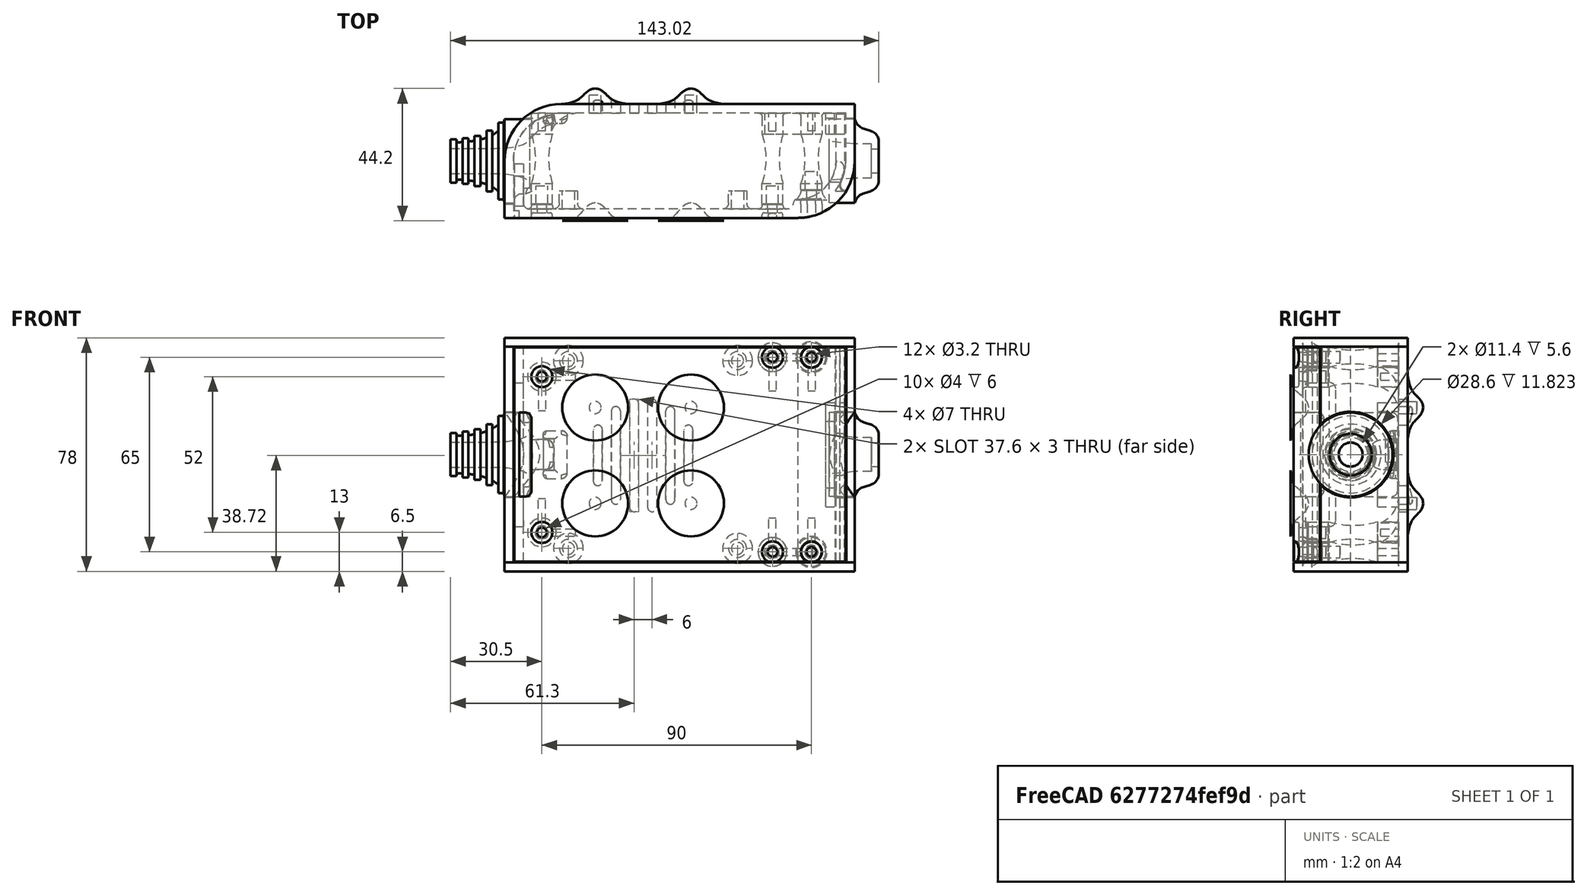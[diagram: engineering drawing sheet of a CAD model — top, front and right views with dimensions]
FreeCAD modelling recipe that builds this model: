
FCSTD DOCUMENT  (FreeCAD 0.19R0.19.2)
Label: enclosure_099
License: All rights reserved
LicenseURL: http://en.wikipedia.org/wiki/All_rights_reserved
objects: Part::Feature×72, Part::Revolution×72, Part::MultiFuse×53, Sketcher::SketchObject×30, Part::Fillet×22, Part::Cylinder×22, Part::Cut×20, Part::Extrusion×19, Part::Box×12, App::MeasureDistance×4
note: 322 computed .brp shape members not serialized (recipe doc carries the construction recipe); baked Part::Feature solids carry a one-line shape summary decoded from their .brp

FEATURE [Sketcher::SketchObject] Sketch  label="topSketch"
  FullyConstrained = true
  sketch-geometry (13):
    g0: LineSegment StartX=117 StartY=19 StartZ=0 EndX=117 EndY=38 EndZ=0
    g1: ArcOfCircle CenterX=98 CenterY=19 CenterZ=0 NormalX=0 NormalY=0 NormalZ=1 AngleXU=0 Radius=19 StartAngle=5.7297 EndAngle=6.28319
    g2: LineSegment StartX=0 StartY=3 StartZ=0 EndX=0 EndY=19 EndZ=0
    g3: LineSegment StartX=19 StartY=38 StartZ=0 EndX=117 EndY=38 EndZ=0
    g4: ArcOfCircle CenterX=19 CenterY=19 CenterZ=0 NormalX=0 NormalY=0 NormalZ=1 AngleXU=0 Radius=19 StartAngle=1.5708 EndAngle=3.14159
    g5: ArcOfCircle CenterX=19 CenterY=19 CenterZ=0 NormalX=0 NormalY=0 NormalZ=1 AngleXU=0 Radius=16 StartAngle=1.5708 EndAngle=3.14159
    g6: ArcOfCircle CenterX=98 CenterY=19 CenterZ=0 NormalX=0 NormalY=0 NormalZ=1 AngleXU=0 Radius=16 StartAngle=5.60905 EndAngle=6.28319
    g7: LineSegment StartX=114 StartY=19 StartZ=0 EndX=114 EndY=35 EndZ=0
    g8: LineSegment StartX=110.5 StartY=9.01251 StartZ=0 EndX=114.163 EndY=9.01251 EndZ=0
    g9: LineSegment StartX=114 StartY=35 StartZ=0 EndX=19 EndY=35 EndZ=0
    g10: LineSegment StartX=0 StartY=3 StartZ=0 EndX=0 EndY=0 EndZ=0
    g11: LineSegment StartX=3 StartY=0 StartZ=0 EndX=0 EndY=0 EndZ=0
    g12: LineSegment StartX=3 StartY=19 StartZ=0 EndX=3 EndY=0 EndZ=0
  constraints (33):
    c: Vertical(g0)
    c: Distance(g0) = 19
    c: Block(g0)
    c: Coincident(g1,g0)
    c: Block(g1)
    c: Vertical(g2)
    c: Block(g2)
    c: Coincident(g3,g0)
    c: Horizontal(g3)
    c: Distance(g3) = 98
    c: Coincident(g4,g3)
    c: Coincident(g4,g2)
    c: Block(g4)
    c: Coincident(g5,g4)
    c: Coincident(g6,g1)
    c: Block(g6)
    c: Block(g5)
    c: Coincident(g7,g6)
    c: Vertical(g7)
    c: Coincident(g8,g6)
    c: Coincident(g8,g1)
    c: Coincident(g9,g7)
    c: Coincident(g9,g5)
    c: Horizontal(g9)
    c: Tangent(g9,g5)
    c: Coincident(g10,g2)
    c: Distance(g10) = 3
    c: Vertical(g10)
    c: Coincident(g11,g10)
    c: Horizontal(g11)
    c: Coincident(g12,g5)
    c: Coincident(g12,g11)
    c: Vertical(g12)
FEATURE [Sketcher::SketchObject] Sketch001  label="bottomSketch"
  FullyConstrained = true
  sketch-geometry (32):
    g0: LineSegment StartX=3.3 StartY=-6.03275e-07 StartZ=0 EndX=98 EndY=-6.03275e-07 EndZ=0
    g1: ArcOfCircle CenterX=98 CenterY=19 CenterZ=0 NormalX=0 NormalY=0 NormalZ=1 AngleXU=0 Radius=19 StartAngle=4.71239 EndAngle=5.71103
    g2: LineSegment StartX=6.3 StartY=8 StartZ=0 EndX=3.3 EndY=8 EndZ=0
    g3: LineSegment StartX=3.3 StartY=8 StartZ=0 EndX=3.3 EndY=-6.03275e-07 EndZ=0
    g4: ArcOfCircle CenterX=8.3 CenterY=5 CenterZ=0 NormalX=0 NormalY=0 NormalZ=1 AngleXU=0 Radius=2 StartAngle=3.14159 EndAngle=4.71239
    g5: LineSegment StartX=6.3 StartY=8 StartZ=0 EndX=6.3 EndY=5 EndZ=0
    g6: ArcOfCircle CenterX=98 CenterY=19 CenterZ=0 NormalX=0 NormalY=0 NormalZ=1 AngleXU=0 Radius=12.7 StartAngle=4.71239 EndAngle=6.28319
    g7: LineSegment StartX=94.7 StartY=3 StartZ=0 EndX=8.3 EndY=3 EndZ=0
    g8-g12: Circle x5 (B-spline internal-alignment scaffolding for g13; pole/knot coordinates omitted)
    g13: BSplineCurve PolesCount=5 KnotsCount=3 Degree=3 IsPeriodic=0
    g14: GeomPoint X=98 Y=6.3 Z=0
    g15: GeomPoint X=96.3938 Y=4.71946 Z=0
    g16: GeomPoint X=94.7 Y=3 Z=0
    g17-g23: Circle x7 (B-spline internal-alignment scaffolding for g24; pole/knot coordinates omitted)
    g24: BSplineCurve PolesCount=7 KnotsCount=5 Degree=3 IsPeriodic=0
    g25-g29: GeomPoint x5 (B-spline internal-alignment scaffolding for g24; pole/knot coordinates omitted)
    g30: ArcOfCircle CenterX=98 CenterY=19 CenterZ=0 NormalX=0 NormalY=0 NormalZ=1 AngleXU=0 Radius=15.7 StartAngle=5.81226 EndAngle=6.28319
    g31: LineSegment StartX=110.7 StartY=19 StartZ=0 EndX=113.7 EndY=19 EndZ=0
  constraints (41):
    c: Horizontal(g0)
    c: Coincident(g1,g0)
    c: Block(g1)
    c: Horizontal(g2)
    c: Distance(g2) = 3
    c: Coincident(g3,g2)
    c: Vertical(g3)
    c: Coincident(g3,g0)
    c: Block(g4)
    c: Block(g2)
    c: Coincident(g5,g2)
    c: Coincident(g5,g4)
    c: Vertical(g5)
    c: Coincident(g6,g1)
    c: Block(g6)
    c: Coincident(g7,g4)
    c: Horizontal(g7)
    c: Block(g0)
    c: Block(g7)
    c: Block(g3)
    c: Coincident(g13,g6)
    c: Weight(g8) = 1
    c: Equal(g8, g9-g12) x4
    c: Coincident(g13,g7)
    c: InternalAlignment(g8-g12 -> g13) x5
    c: InternalAlignment(g14,g13)
    c: InternalAlignment(g15,g13)
    c: InternalAlignment(g16,g13)
    c: Block(g13)
    c: Weight(g17) = 1
    c: Equal(g17, g18-g23) x6
    c: Coincident(g24,g1)
    c: InternalAlignment(g17-g23 -> g24) x7
    c: InternalAlignment(g25-g29 -> g24) x5
    c: Block(g24)
    c: Coincident(g30,g24)
    c: Coincident(g31,g6)
    c: Coincident(g31,g30)
    c: Horizontal(g31)
    c: Block(g31)
    c: Block(g30)
FEATURE [Part::Extrusion] Extrude  label="top"
  Base = -> Sketch
  Dir = (0,0,1)
  DirMode = 2
  FaceMakerClass = Part::FaceMakerBullseye
  LengthFwd = 72
  LengthRev = 0
  Solid = true
  Symmetric = false
FEATURE [Part::Extrusion] Extrude001  label="bottom"
  Base = -> Sketch001
  Dir = (0,0,1)
  DirMode = 2
  FaceMakerClass = Part::FaceMakerBullseye
  LengthFwd = 71.4
  LengthRev = 0
  Placement = pos=(0,0,0.3) rot=(0,0,1;0rad)
  Solid = true
  Symmetric = false
FEATURE [Sketcher::SketchObject] Sketch002  label="topSketch001"
  FullyConstrained = true
  sketch-geometry (6):
    g0: LineSegment StartX=19 StartY=38 StartZ=0 EndX=117 EndY=38 EndZ=0
    g1: ArcOfCircle CenterX=19 CenterY=19 CenterZ=0 NormalX=0 NormalY=0 NormalZ=1 AngleXU=0 Radius=19 StartAngle=1.5708 EndAngle=3.14159
    g2: LineSegment StartX=117 StartY=38 StartZ=0 EndX=117 EndY=19 EndZ=0
    g3: LineSegment StartX=98 StartY=1.0161e-12 StartZ=0 EndX=5.22862e-06 EndY=1.0161e-12 EndZ=0
    g4: LineSegment StartX=5.22862e-06 StartY=19 StartZ=0 EndX=5.22862e-06 EndY=1.0161e-12 EndZ=0
    g5: ArcOfCircle CenterX=98 CenterY=19 CenterZ=0 NormalX=0 NormalY=0 NormalZ=1 AngleXU=0 Radius=19 StartAngle=4.71239 EndAngle=6.28319
  constraints (16):
    c: Horizontal(g0)
    c: Distance(g0) = 98
    c: Coincident(g1,g0)
    c: Block(g1)
    c: Coincident(g2,g0)
    c: Vertical(g2)
    c: Distance(g2) = 19
    c: Horizontal(g3)
    c: Coincident(g4,g1)
    c: Vertical(g4)
    c: Coincident(g3,g4)
    c: Block(g3)
    c: Coincident(g5,g2)
    c: Coincident(g5,g3)
    c: Block(g0)
    c: Block(g5)
FEATURE [Part::Extrusion] Extrude002  label="sideA"
  Base = -> Sketch002
  Dir = (0,0,1)
  DirMode = 2
  FaceMakerClass = Part::FaceMakerBullseye
  LengthFwd = 3
  LengthRev = 0
  Placement = pos=(0,0,-3) rot=(0,0,1;0rad)
  Solid = true
  Symmetric = false
FEATURE [Sketcher::SketchObject] Sketch003  label="topSketch002"
  FullyConstrained = true
  sketch-geometry (6):
    g0: LineSegment StartX=19 StartY=38 StartZ=0 EndX=117 EndY=38 EndZ=0
    g1: ArcOfCircle CenterX=19 CenterY=19 CenterZ=0 NormalX=0 NormalY=0 NormalZ=1 AngleXU=0 Radius=19 StartAngle=1.5708 EndAngle=3.14159
    g2: LineSegment StartX=117 StartY=38 StartZ=0 EndX=117 EndY=19 EndZ=0
    g3: LineSegment StartX=98 StartY=1.0161e-12 StartZ=0 EndX=5.22862e-06 EndY=1.0161e-12 EndZ=0
    g4: LineSegment StartX=5.22862e-06 StartY=19 StartZ=0 EndX=5.22862e-06 EndY=1.0161e-12 EndZ=0
    g5: ArcOfCircle CenterX=98 CenterY=19 CenterZ=0 NormalX=0 NormalY=0 NormalZ=1 AngleXU=0 Radius=19 StartAngle=4.71239 EndAngle=6.28319
  constraints (16):
    c: Horizontal(g0)
    c: Distance(g0) = 98
    c: Coincident(g1,g0)
    c: Block(g1)
    c: Coincident(g2,g0)
    c: Vertical(g2)
    c: Distance(g2) = 19
    c: Horizontal(g3)
    c: Coincident(g4,g1)
    c: Vertical(g4)
    c: Coincident(g3,g4)
    c: Block(g3)
    c: Coincident(g5,g2)
    c: Coincident(g5,g3)
    c: Block(g0)
    c: Block(g5)
FEATURE [Part::Extrusion] Extrude003  label="sideB"
  Base = -> Sketch003
  Dir = (0,0,1)
  DirMode = 2
  FaceMakerClass = Part::FaceMakerBullseye
  LengthFwd = 3
  LengthRev = 0
  Placement = pos=(0,0,72) rot=(0,0,1;0rad)
  Solid = true
  Symmetric = false
FEATURE [Sketcher::SketchObject] Sketch004
  FullyConstrained = true
  MapMode = 3
  Placement = pos=(0,0,0) rot=(1,0,0;1.5708rad)
  Support = -> [Extrude]
  sketch-geometry (8):
    g0: Circle CenterX=80.351 CenterY=-67.6202 CenterZ=0 NormalX=0 NormalY=0 NormalZ=1 AngleXU=0 Radius=2
    g1: Circle CenterX=80.351 CenterY=-67.6202 CenterZ=0 NormalX=0 NormalY=0 NormalZ=1 AngleXU=0 Radius=3
    g2: Circle CenterX=80.351 CenterY=-4.92017 CenterZ=0 NormalX=0 NormalY=0 NormalZ=1 AngleXU=0 Radius=2
    g3: Circle CenterX=80.351 CenterY=-4.92017 CenterZ=0 NormalX=0 NormalY=0 NormalZ=1 AngleXU=0 Radius=3
    g4: Circle CenterX=23.851 CenterY=-4.92017 CenterZ=0 NormalX=0 NormalY=0 NormalZ=1 AngleXU=0 Radius=2
    g5: Circle CenterX=23.851 CenterY=-4.92017 CenterZ=0 NormalX=0 NormalY=0 NormalZ=1 AngleXU=0 Radius=3
    g6: Circle CenterX=23.851 CenterY=-67.6202 CenterZ=0 NormalX=0 NormalY=0 NormalZ=1 AngleXU=0 Radius=2
    g7: Circle CenterX=23.851 CenterY=-67.6202 CenterZ=0 NormalX=0 NormalY=0 NormalZ=1 AngleXU=0 Radius=3
  constraints (8):
    c: Block(g3)
    c: Block(g2)
    c: Block(g1)
    c: Block(g0)
    c: Block(g6)
    c: Block(g7)
    c: Block(g4)
    c: Block(g5)
FEATURE [Part::Extrusion] Extrude004
  Base = -> Sketch004
  Dir = (0,-1,2e-16)
  DirMode = 2
  FaceMakerClass = Part::FaceMakerBullseye
  LengthFwd = 6
  LengthRev = 0
  Placement = pos=(0,9,0) rot=(0,0,1;0rad)
  Solid = true
  Symmetric = false
FEATURE [Sketcher::SketchObject] Sketch005
  FullyConstrained = true
  MapMode = 3
  Placement = pos=(0,0,0) rot=(1,0,0;1.5708rad)
  Support = -> [Extrude]
  sketch-geometry (8):
    g0: Circle CenterX=80.351 CenterY=-67.6202 CenterZ=0 NormalX=0 NormalY=0 NormalZ=1 AngleXU=0 Radius=3
    g1: Circle CenterX=80.351 CenterY=-4.92017 CenterZ=0 NormalX=0 NormalY=0 NormalZ=1 AngleXU=0 Radius=3
    g2: Circle CenterX=23.851 CenterY=-4.92017 CenterZ=0 NormalX=0 NormalY=0 NormalZ=1 AngleXU=0 Radius=3
    g3: Circle CenterX=23.851 CenterY=-67.6202 CenterZ=0 NormalX=0 NormalY=0 NormalZ=1 AngleXU=0 Radius=3
    g4: Circle CenterX=23.851 CenterY=-67.6202 CenterZ=0 NormalX=0 NormalY=0 NormalZ=1 AngleXU=0 Radius=5
    g5: Circle CenterX=80.351 CenterY=-67.6202 CenterZ=0 NormalX=0 NormalY=0 NormalZ=1 AngleXU=0 Radius=5
    g6: Circle CenterX=23.851 CenterY=-4.92017 CenterZ=0 NormalX=0 NormalY=0 NormalZ=1 AngleXU=0 Radius=5
    g7: Circle CenterX=80.351 CenterY=-4.92017 CenterZ=0 NormalX=0 NormalY=0 NormalZ=1 AngleXU=0 Radius=5
  constraints (8):
    c: Block(g1)
    c: Block(g0)
    c: Block(g3)
    c: Block(g2)
    c: Block(g5)
    c: Block(g4)
    c: Block(g6)
    c: Block(g7)
FEATURE [Part::Extrusion] Extrude005
  Base = -> Sketch005
  Dir = (0,-1,2e-16)
  DirMode = 2
  FaceMakerClass = Part::FaceMakerBullseye
  LengthFwd = 2
  LengthRev = 0
  Solid = true
  Symmetric = false
FEATURE [Sketcher::SketchObject] Sketch006
  FullyConstrained = true
  MapMode = 3
  Placement = pos=(0,0,0) rot=(1,0,0;1.5708rad)
  sketch-geometry (8):
    g0: Circle CenterX=80.351 CenterY=-67.6202 CenterZ=0 NormalX=0 NormalY=0 NormalZ=1 AngleXU=0 Radius=3
    g1: Circle CenterX=80.351 CenterY=-4.92017 CenterZ=0 NormalX=0 NormalY=0 NormalZ=1 AngleXU=0 Radius=3
    g2: Circle CenterX=23.851 CenterY=-4.92017 CenterZ=0 NormalX=0 NormalY=0 NormalZ=1 AngleXU=0 Radius=3
    g3: Circle CenterX=23.851 CenterY=-67.6202 CenterZ=0 NormalX=0 NormalY=0 NormalZ=1 AngleXU=0 Radius=3
    g4: Circle CenterX=23.851 CenterY=-67.6202 CenterZ=0 NormalX=0 NormalY=0 NormalZ=1 AngleXU=0 Radius=5
    g5: Circle CenterX=80.351 CenterY=-67.6202 CenterZ=0 NormalX=0 NormalY=0 NormalZ=1 AngleXU=0 Radius=5
    g6: Circle CenterX=23.851 CenterY=-4.92017 CenterZ=0 NormalX=0 NormalY=0 NormalZ=1 AngleXU=0 Radius=5
    g7: Circle CenterX=80.351 CenterY=-4.92017 CenterZ=0 NormalX=0 NormalY=0 NormalZ=1 AngleXU=0 Radius=5
  constraints (8):
    c: Block(g1)
    c: Block(g0)
    c: Block(g3)
    c: Block(g2)
    c: Block(g5)
    c: Block(g4)
    c: Block(g6)
    c: Block(g7)
FEATURE [Part::Extrusion] Extrude007
  Base = -> Sketch006
  Dir = (0,-1,2e-16)
  DirMode = 2
  FaceMakerClass = Part::FaceMakerBullseye
  LengthFwd = 2
  LengthRev = 0
  Solid = true
  Symmetric = false
FEATURE [Part::Fillet] Fillet
  Base = -> Extrude007
  Edges = 4 edges r=1.99: [Edge6,Edge12,Edge18,Edge24]
FEATURE [Part::Cut] Cut
  Base = -> Extrude005
  Placement = pos=(0,5,0) rot=(0,0,1;0rad)
  Tool = -> Fillet
FEATURE [Part::MultiFuse] Fusion  label="pCBScrews"
  Placement = pos=(-2.5,0,72.3) rot=(0,0,1;0rad)
  Shapes = -> [Extrude004,Cut]
FEATURE [App::MeasureDistance] Distance  label="Distance: 0.69 mm"
  Distance = 0.685967
  P1 = (24.0138,2.9647,0.3)
  P2 = (23.8901,3,-0.373787)
FEATURE [App::MeasureDistance] Distance001  label="Distance: 0.53 mm"
  Distance = 0.533607
  P1 = (80.2939,3,72.2334)
  P2 = (80.281,2.99661,71.7)
FEATURE [Part::Fillet] Fillet001
  Base = -> Extrude001
  Edges = 1 edges r=2.4: [Edge17]
FEATURE [Part::Fillet] Fillet002  label="bottom001"
  Base = -> Fillet001
  Edges = 1 edges r=2.4: [Edge36]
FEATURE [Part::Fillet] Fillet003  label="top001"
  Base = -> Extrude
  Edges = 1 edges r=2: [Edge1]
FEATURE [Sketcher::SketchObject] Sketch007
  FullyConstrained = true
  sketch-geometry (16):
    g0: LineSegment StartX=4 StartY=0 StartZ=0 EndX=4 EndY=2.4 EndZ=0
    g1: LineSegment StartX=4 StartY=2.4 StartZ=0 EndX=7 EndY=2.4 EndZ=0
    g2: LineSegment StartX=4 StartY=0 StartZ=0 EndX=5.7 EndY=0 EndZ=0
    g3: LineSegment StartX=5.7 StartY=0 StartZ=0 EndX=5.7 EndY=-5.6 EndZ=0
    g4-g8: Circle x5 (B-spline internal-alignment scaffolding for g9; pole/knot coordinates omitted)
    g9: BSplineCurve PolesCount=5 KnotsCount=3 Degree=3 IsPeriodic=0
    g10: GeomPoint X=7 Y=2.4 Z=0
    g11: GeomPoint X=10.4582 Y=-1.55472 Z=0
    g12: GeomPoint X=14 Y=-5.6 Z=0
    g13: LineSegment StartX=14 StartY=-5.6 StartZ=0 EndX=14 EndY=-14.1 EndZ=0
    g14: LineSegment StartX=14 StartY=-14.1 StartZ=0 EndX=6.5 EndY=-14.1 EndZ=0
    g15: LineSegment StartX=5.7 StartY=-5.6 StartZ=0 EndX=6.5 EndY=-14.1 EndZ=0
  constraints (28):
    c: Distance(g0) = 2.4
    c: Vertical(g0)
    c: Block(g0)
    c: Coincident(g1,g0)
    c: Horizontal(g1)
    c: Distance(g1) = 3
    c: Coincident(g2,g0)
    c: Horizontal(g2)
    c: Distance(g2) = 1.7
    c: Coincident(g3,g2)
    c: Vertical(g3)
    c: Distance(g3) = 5.6
    c: Coincident(g9,g1)
    c: Weight(g4) = 1
    c: Equal(g4, g5-g8) x4
    c: InternalAlignment(g4-g8 -> g9) x5
    c: InternalAlignment(g10,g9)
    c: InternalAlignment(g11,g9)
    c: InternalAlignment(g12,g9)
    c: Block(g9)
    c: Coincident(g13,g9)
    c: Vertical(g13)
    c: Distance(g13) = 8.5
    c: Coincident(g14,g13)
    c: Horizontal(g14)
    c: Distance(g14) = 7.5
    c: Coincident(g15,g3)
    c: Coincident(g15,g14)
FEATURE [Part::Feature] Face
  shape: bbox 10 x 16.5 x 2e-07 mm, 1 faces, 0 solids (baked)
FEATURE [Part::Revolution] Revolve  label="plugHousing"
  Angle = 360
  Axis = (0,1,0)
  Base = (0,0,0)
  FaceMakerClass = Part::FaceMakerBullseye
  Placement = pos=(0,0,36.15) rot=(0,0,1;0rad)
  Solid = false
  Source = -> Face
  Symmetric = false
FEATURE [Part::Feature] Face001
  shape: bbox 10 x 16.5 x 2e-07 mm, 1 faces, 0 solids (baked)
FEATURE [Part::Revolution] Revolve001  label="plugHousing001"
  Angle = 360
  Axis = (0,1,0)
  Base = (0,0,0)
  FaceMakerClass = Part::FaceMakerBullseye
  Placement = pos=(0,0,36.15) rot=(0,0,1;0rad)
  Solid = false
  Source = -> Face001
  Symmetric = false
FEATURE [Part::MultiFuse] Fusion001  label="plugHousing002"
  Placement = pos=(0,0,0) rot=(0,0,1;1.5708rad)
  Shapes = -> [Revolve001,Revolve]
FEATURE [Part::Feature] Face002
  shape: bbox 10 x 16.5 x 2e-07 mm, 1 faces, 0 solids (baked)
FEATURE [Part::Revolution] Revolve003  label="plugHousing005"
  Angle = 360
  Axis = (0,1,0)
  Base = (0,0,0)
  FaceMakerClass = Part::FaceMakerBullseye
  Placement = pos=(0,0,36.15) rot=(0,0,1;0rad)
  Solid = false
  Source = -> Face002
  Symmetric = false
FEATURE [Part::Feature] Face003
  shape: bbox 10 x 16.5 x 2e-07 mm, 1 faces, 0 solids (baked)
FEATURE [Part::Revolution] Revolve002  label="plugHousing003"
  Angle = 360
  Axis = (0,1,0)
  Base = (0,0,0)
  FaceMakerClass = Part::FaceMakerBullseye
  Placement = pos=(0,0,36.15) rot=(0,0,1;0rad)
  Solid = false
  Source = -> Face003
  Symmetric = false
FEATURE [Part::MultiFuse] Fusion002  label="plugHousing004"
  Placement = pos=(0,0,0) rot=(0,0,1;1.5708rad)
  Shapes = -> [Revolve002,Revolve003]
FEATURE [Part::MultiFuse] Fusion003  label="plugHousing006"
  Placement = pos=(0,19,0) rot=(0,0,1;3.14159rad)
  Shapes = -> [Fusion002,Fusion001]
FEATURE [Part::Feature] Face004
  shape: bbox 10 x 16.5 x 2e-07 mm, 1 faces, 0 solids (baked)
FEATURE [Part::Revolution] Revolve006  label="plugHousing010"
  Angle = 360
  Axis = (0,1,0)
  Base = (0,0,0)
  FaceMakerClass = Part::FaceMakerBullseye
  Placement = pos=(0,0,36.15) rot=(0,0,1;0rad)
  Solid = false
  Source = -> Face004
  Symmetric = false
FEATURE [Part::Feature] Face005
  shape: bbox 10 x 16.5 x 2e-07 mm, 1 faces, 0 solids (baked)
FEATURE [Part::Revolution] Revolve007  label="plugHousing011"
  Angle = 360
  Axis = (0,1,0)
  Base = (0,0,0)
  FaceMakerClass = Part::FaceMakerBullseye
  Placement = pos=(0,0,36.15) rot=(0,0,1;0rad)
  Solid = false
  Source = -> Face005
  Symmetric = false
FEATURE [Part::Feature] Face006
  shape: bbox 10 x 16.5 x 2e-07 mm, 1 faces, 0 solids (baked)
FEATURE [Part::Revolution] Revolve004  label="plugHousing007"
  Angle = 360
  Axis = (0,1,0)
  Base = (0,0,0)
  FaceMakerClass = Part::FaceMakerBullseye
  Placement = pos=(0,0,36.15) rot=(0,0,1;0rad)
  Solid = false
  Source = -> Face006
  Symmetric = false
FEATURE [Part::MultiFuse] Fusion004  label="plugHousing009"
  Placement = pos=(0,0,0) rot=(0,0,1;1.5708rad)
  Shapes = -> [Revolve004,Revolve007]
FEATURE [Part::Feature] Face007
  shape: bbox 10 x 16.5 x 2e-07 mm, 1 faces, 0 solids (baked)
FEATURE [Part::Revolution] Revolve005  label="plugHousing008"
  Angle = 360
  Axis = (0,1,0)
  Base = (0,0,0)
  FaceMakerClass = Part::FaceMakerBullseye
  Placement = pos=(0,0,36.15) rot=(0,0,1;0rad)
  Solid = false
  Source = -> Face007
  Symmetric = false
FEATURE [Part::MultiFuse] Fusion005  label="plugHousing012"
  Placement = pos=(0,0,0) rot=(0,0,1;1.5708rad)
  Shapes = -> [Revolve006,Revolve005]
FEATURE [Part::MultiFuse] Fusion006  label="plugHousing013"
  Placement = pos=(0,19,0) rot=(0,0,1;3.14159rad)
  Shapes = -> [Fusion005,Fusion004]
FEATURE [Part::MultiFuse] Fusion007  label="plugHousing014"
  Placement = pos=(122.621,0,-0.15) rot=(0,0,1;0rad)
  Shapes = -> [Fusion003,Fusion006]
FEATURE [Part::Cylinder] Cylinder002
  Angle = 360
  AttacherType = Attacher::AttachEngine3D
  Height = 20
  Placement = pos=(0,0,36.15) rot=(0,0,1;0rad)
  Radius = 4
FEATURE [Part::Cylinder] Cylinder003
  Angle = 360
  AttacherType = Attacher::AttachEngine3D
  Height = 10
  Placement = pos=(0,0,36.15) rot=(0,0,1;0rad)
  Radius = 4
FEATURE [Part::MultiFuse] Fusion009  label="removeToCreateHoleForPlugHousing"
  Placement = pos=(70,19,36.15) rot=(0,1,0;1.5708rad)
  Shapes = -> [Cylinder002,Cylinder003]
FEATURE [Part::Cylinder] Cylinder004
  Angle = 360
  AttacherType = Attacher::AttachEngine3D
  Height = 20
  Placement = pos=(0,0,36.15) rot=(0,0,1;0rad)
  Radius = 4
FEATURE [Part::Cylinder] Cylinder005
  Angle = 360
  AttacherType = Attacher::AttachEngine3D
  Height = 10
  Placement = pos=(0,0,36.15) rot=(0,0,1;0rad)
  Radius = 4
FEATURE [Part::MultiFuse] Fusion010  label="removeToCreateHoleForPlugHousing001"
  Placement = pos=(70,19,36.15) rot=(0,1,0;1.5708rad)
  Shapes = -> [Cylinder004,Cylinder005]
FEATURE [Part::Cut] Cut001
  Base = -> Fillet003
  Tool = -> Fusion010
FEATURE [Part::Cut] Cut002  label="Bottom"
  Base = -> Fillet002
  Tool = -> Fusion009
FEATURE [Part::Feature] Face008
  shape: bbox 10 x 16.5 x 2e-07 mm, 1 faces, 0 solids (baked)
FEATURE [Part::Revolution] Revolve011  label="plugHousing021"
  Angle = 360
  Axis = (0,1,0)
  Base = (0,0,0)
  FaceMakerClass = Part::FaceMakerBullseye
  Placement = pos=(0,0,36.15) rot=(0,0,1;0rad)
  Solid = false
  Source = -> Face008
  Symmetric = false
FEATURE [Part::Feature] Face009
  shape: bbox 10 x 16.5 x 2e-07 mm, 1 faces, 0 solids (baked)
FEATURE [Part::Revolution] Revolve012  label="plugHousing022"
  Angle = 360
  Axis = (0,1,0)
  Base = (0,0,0)
  FaceMakerClass = Part::FaceMakerBullseye
  Placement = pos=(0,0,36.15) rot=(0,0,1;0rad)
  Solid = false
  Source = -> Face009
  Symmetric = false
FEATURE [Part::Feature] Face010 .. Face013  x4 (patterned run collapsed; names and placements below)
  shape: bbox 10 x 16.5 x 2e-07 mm, 1 faces, 0 solids (baked)
FEATURE [Part::Revolution] Revolve015  label="plugHousing027"
  Angle = 360
  Axis = (0,1,0)
  Base = (0,0,0)
  FaceMakerClass = Part::FaceMakerBullseye
  Placement = pos=(0,0,36.15) rot=(0,0,1;0rad)
  Solid = false
  Source = -> Face013
  Symmetric = false
FEATURE [Part::Feature] Face014
  shape: bbox 10 x 16.5 x 2e-07 mm, 1 faces, 0 solids (baked)
FEATURE [Part::Feature] Face015
  shape: bbox 10 x 16.5 x 2e-07 mm, 1 faces, 0 solids (baked)
FEATURE [Part::Feature] Face016
  shape: bbox 10 x 16.5 x 2e-07 mm, 1 faces, 0 solids (baked)
FEATURE [Part::Revolution] Revolve019  label="plugHousing033"
  Angle = 360
  Axis = (0,1,0)
  Base = (0,0,0)
  FaceMakerClass = Part::FaceMakerBullseye
  Placement = pos=(0,0,36.15) rot=(0,0,1;0rad)
  Solid = false
  Source = -> Face016
  Symmetric = false
FEATURE [Part::Feature] Face017
  shape: bbox 10 x 16.5 x 2e-07 mm, 1 faces, 0 solids (baked)
FEATURE [Part::Revolution] Revolve020  label="plugHousing034"
  Angle = 360
  Axis = (0,1,0)
  Base = (0,0,0)
  FaceMakerClass = Part::FaceMakerBullseye
  Placement = pos=(0,0,36.15) rot=(0,0,1;0rad)
  Solid = false
  Source = -> Face017
  Symmetric = false
FEATURE [Part::Feature] Face018
  shape: bbox 10 x 16.5 x 2e-07 mm, 1 faces, 0 solids (baked)
FEATURE [Part::Revolution] Revolve016  label="plugHousing030"
  Angle = 360
  Axis = (0,1,0)
  Base = (0,0,0)
  FaceMakerClass = Part::FaceMakerBullseye
  Placement = pos=(0,0,36.15) rot=(0,0,1;0rad)
  Solid = false
  Source = -> Face018
  Symmetric = false
FEATURE [Part::MultiFuse] Fusion020  label="plugHousing038"
  Placement = pos=(0,0,0) rot=(0,0,1;1.5708rad)
  Shapes = -> [Revolve016,Revolve020]
FEATURE [Part::Feature] Face019
  shape: bbox 10 x 16.5 x 2e-07 mm, 1 faces, 0 solids (baked)
FEATURE [Part::Feature] Face020
  shape: bbox 10 x 16.5 x 2e-07 mm, 1 faces, 0 solids (baked)
FEATURE [Part::Revolution] Revolve017  label="plugHousing031"
  Angle = 360
  Axis = (0,1,0)
  Base = (0,0,0)
  FaceMakerClass = Part::FaceMakerBullseye
  Placement = pos=(0,0,36.15) rot=(0,0,1;0rad)
  Solid = false
  Source = -> Face020
  Symmetric = false
FEATURE [Part::MultiFuse] Fusion021  label="plugHousing039"
  Placement = pos=(0,0,0) rot=(0,0,1;1.5708rad)
  Shapes = -> [Revolve019,Revolve017]
FEATURE [Part::MultiFuse] Fusion023  label="plugHousing041"
  Placement = pos=(0,19,0) rot=(0,0,1;3.14159rad)
  Shapes = -> [Fusion021,Fusion020]
FEATURE [Part::Revolution] Revolve022  label="plugHousing043"
  Angle = 360
  Axis = (0,1,0)
  Base = (0,0,0)
  FaceMakerClass = Part::FaceMakerBullseye
  Placement = pos=(0,0,36.15) rot=(0,0,1;0rad)
  Solid = false
  Source = -> Face019
  Symmetric = false
FEATURE [Part::Feature] Face021
  shape: bbox 10 x 16.5 x 2e-07 mm, 1 faces, 0 solids (baked)
FEATURE [Part::Revolution] Revolve023  label="plugHousing044"
  Angle = 360
  Axis = (0,1,0)
  Base = (0,0,0)
  FaceMakerClass = Part::FaceMakerBullseye
  Placement = pos=(0,0,36.15) rot=(0,0,1;0rad)
  Solid = false
  Source = -> Face021
  Symmetric = false
FEATURE [Part::Feature] Face022
  shape: bbox 10 x 16.5 x 2e-07 mm, 1 faces, 0 solids (baked)
FEATURE [Part::Revolution] Revolve018  label="plugHousing032"
  Angle = 360
  Axis = (0,1,0)
  Base = (0,0,0)
  FaceMakerClass = Part::FaceMakerBullseye
  Placement = pos=(0,0,36.15) rot=(0,0,1;0rad)
  Solid = false
  Source = -> Face022
  Symmetric = false
FEATURE [Part::MultiFuse] Fusion022  label="plugHousing040"
  Placement = pos=(0,0,0) rot=(0,0,1;1.5708rad)
  Shapes = -> [Revolve018,Revolve023]
FEATURE [Part::Feature] Face023
  shape: bbox 10 x 16.5 x 2e-07 mm, 1 faces, 0 solids (baked)
FEATURE [Part::Revolution] Revolve021  label="plugHousing035"
  Angle = 360
  Axis = (0,1,0)
  Base = (0,0,0)
  FaceMakerClass = Part::FaceMakerBullseye
  Placement = pos=(0,0,36.15) rot=(0,0,1;0rad)
  Solid = false
  Source = -> Face023
  Symmetric = false
FEATURE [Part::MultiFuse] Fusion018  label="plugHousing036"
  Placement = pos=(0,0,0) rot=(0,0,1;1.5708rad)
  Shapes = -> [Revolve022,Revolve021]
FEATURE [Part::MultiFuse] Fusion019  label="plugHousing037"
  Placement = pos=(0,19,0) rot=(0,0,1;3.14159rad)
  Shapes = -> [Fusion018,Fusion022]
FEATURE [Part::MultiFuse] Fusion024  label="plugHousing042"
  Placement = pos=(122.621,0,-0.15) rot=(0,0,1;0rad)
  Shapes = -> [Fusion023,Fusion019]
FEATURE [Part::Cylinder] Cylinder006
  Angle = 360
  AttacherType = Attacher::AttachEngine3D
  Height = 20
  Placement = pos=(0,0,36.15) rot=(0,0,1;0rad)
  Radius = 14.3
FEATURE [Part::Cylinder] Cylinder007
  Angle = 360
  AttacherType = Attacher::AttachEngine3D
  Height = 10
  Placement = pos=(0,0,36.15) rot=(0,0,1;0rad)
  Radius = 4
FEATURE [Part::MultiFuse] Fusion026  label="removeToCreteHoleForPlugHousing"
  Placement = pos=(70,19,36) rot=(0,1,0;1.5708rad)
  Shapes = -> [Cylinder006,Cylinder007]
FEATURE [Part::Box] Box001  label="Cube001"
  AttacherType = Attacher::AttachEngine3D
  Height = 28
  Length = 3
  Placement = pos=(110.7,19,22) rot=(0,0,1;0rad)
  Width = 15.7
FEATURE [Part::Cut] Cut003  label="top002"
  Base = -> Cut001
  Tool = -> Fusion007
FEATURE [Part::Revolution] Revolve008  label="plugHousing015"
  Angle = 360
  Axis = (0,1,0)
  Base = (0,0,0)
  FaceMakerClass = Part::FaceMakerBullseye
  Placement = pos=(0,0,36.15) rot=(0,0,1;0rad)
  Solid = false
  Source = -> Face010
  Symmetric = false
FEATURE [Part::MultiFuse] Fusion013  label="plugHousing020"
  Placement = pos=(0,0,0) rot=(0,0,1;1.5708rad)
  Shapes = -> [Revolve008,Revolve012]
FEATURE [Part::Cut] Cut004  label="top003"
  Base = -> Cut003
  Placement = pos=(1,0,0) rot=(0,0,1;0rad)
  Tool = -> Fusion026
FEATURE [Part::Cylinder] Cylinder008
  Angle = 360
  AttacherType = Attacher::AttachEngine3D
  Height = 20
  Placement = pos=(0,0,36.15) rot=(0,0,1;0rad)
  Radius = 10.3
FEATURE [Part::Cylinder] Cylinder009
  Angle = 360
  AttacherType = Attacher::AttachEngine3D
  Height = 10
  Placement = pos=(0,0,36.15) rot=(0,0,1;0rad)
  Radius = 4
FEATURE [Part::MultiFuse] Fusion027  label="removeToCreteHoleForPlugHousing001"
  Placement = pos=(70,19,36) rot=(0,1,0;1.5708rad)
  Shapes = -> [Cylinder008,Cylinder009]
FEATURE [Part::Cut] Cut005  label="plugHousingTab"
  Base = -> Box001
  Tool = -> Fusion027
FEATURE [Part::MultiFuse] Fusion028  label="plugHousing045"
  Shapes = -> [Fusion024,Cut005]
FEATURE [Part::Box] Box002  label="Cube002"
  AttacherType = Attacher::AttachEngine3D
  Height = 28.8
  Length = 3
  Placement = pos=(107.3,28,21.6) rot=(0,0,1;0rad)
  Width = 7
FEATURE [Part::Box] Box003  label="Cube003"
  AttacherType = Attacher::AttachEngine3D
  Height = 3
  Length = 6.4
  Placement = pos=(107.3,28,18.6) rot=(0,0,1;0rad)
  Width = 7
FEATURE [Part::Box] Box004  label="Cube004"
  AttacherType = Attacher::AttachEngine3D
  Height = 3
  Length = 6.4
  Placement = pos=(107.3,28,50.4) rot=(0,0,1;0rad)
  Width = 7
FEATURE [Part::MultiFuse] Fusion029  label="plugHousingBracketHolder"
  Shapes = -> [Box004,Box002,Box003]
FEATURE [Part::Cylinder] Cylinder010
  Angle = 360
  AttacherType = Attacher::AttachEngine3D
  Height = 20
  Placement = pos=(0,0,36.15) rot=(0,0,1;0rad)
  Radius = 14.3
FEATURE [Part::Cylinder] Cylinder011
  Angle = 360
  AttacherType = Attacher::AttachEngine3D
  Height = 10
  Placement = pos=(0,0,36.15) rot=(0,0,1;0rad)
  Radius = 4
FEATURE [Part::MultiFuse] Fusion030  label="removeToCreteHoleForPlugHousing002"
  Placement = pos=(70,19,36) rot=(0,1,0;1.5708rad)
  Shapes = -> [Cylinder010,Cylinder011]
FEATURE [Part::Cut] Cut006  label="plugHousingBracketHolder001"
  Base = -> Fusion029
  Tool = -> Fusion030
FEATURE [Part::Cylinder] Cylinder012
  Angle = 360
  AttacherType = Attacher::AttachEngine3D
  Height = 20
  Placement = pos=(0,0,36.15) rot=(0,0,1;0rad)
  Radius = 7
FEATURE [Part::Cylinder] Cylinder013
  Angle = 360
  AttacherType = Attacher::AttachEngine3D
  Height = 10
  Placement = pos=(0,0,36.15) rot=(0,0,1;0rad)
  Radius = 4
FEATURE [Part::MultiFuse] Fusion032  label="removeToCreteHoleForPlugHousing003"
  Placement = pos=(70,19,36) rot=(0,1,0;1.5708rad)
  Shapes = -> [Cylinder012,Cylinder013]
FEATURE [Part::Cut] Cut007  label="bottom002"
  Base = -> Cut002
  Tool = -> Fusion032
FEATURE [Sketcher::SketchObject] Sketch008
  FullyConstrained = true
  sketch-geometry (54):
    g0: LineSegment StartX=-4.2 StartY=0 StartZ=0 EndX=-6.2 EndY=0 EndZ=0
    g1: LineSegment StartX=-14 StartY=-18 StartZ=0 EndX=-14 EndY=-26.5 EndZ=0
    g2: LineSegment StartX=-4.2 StartY=0 StartZ=0 EndX=-4.2 EndY=-13.4877 EndZ=0
    g3: Circle CenterX=-4.2 CenterY=-13.4877 CenterZ=0 NormalX=0 NormalY=0 NormalZ=1 AngleXU=0 Radius=1
    g4: Circle CenterX=-4.2 CenterY=-26.5 CenterZ=0 NormalX=0 NormalY=0 NormalZ=1 AngleXU=0 Radius=1
    g5: Circle CenterX=-8.2 CenterY=-26.5 CenterZ=0 NormalX=0 NormalY=0 NormalZ=1 AngleXU=0 Radius=1
    g6: BSplineCurve PolesCount=3 KnotsCount=2 Degree=2 IsPeriodic=0
    g7: GeomPoint X=-4.2 Y=-13.4877 Z=0
    g8: GeomPoint X=-8.2 Y=-26.5 Z=0
    g9: LineSegment StartX=-14 StartY=-26.5 StartZ=0 EndX=-8.2 EndY=-26.5 EndZ=0
    g10: LineSegment StartX=-10.15 StartY=-12 StartZ=0 EndX=-10.15 EndY=-14 EndZ=0
    g11: LineSegment StartX=-12.8401 StartY=-16 StartZ=0 EndX=-10.1571 EndY=-16 EndZ=0
    g12: LineSegment StartX=-10.15 StartY=-14 StartZ=0 EndX=-8.70761 EndY=-14 EndZ=0
    g13: LineSegment StartX=-12.8401 StartY=-16 StartZ=0 EndX=-12.8401 EndY=-17.6958 EndZ=0
    g14: LineSegment StartX=-10.15 StartY=-12 StartZ=0 EndX=-7.79258 EndY=-12 EndZ=0
    g15: Circle CenterX=-6.2215 CenterY=-2 CenterZ=0 NormalX=0 NormalY=0 NormalZ=1 AngleXU=0 Radius=1
    g16: Circle CenterX=-6.22762 CenterY=-2.58724 CenterZ=0 NormalX=0 NormalY=0 NormalZ=1 AngleXU=0 Radius=1
    g17: Circle CenterX=-6.32538 CenterY=-4 CenterZ=0 NormalX=0 NormalY=0 NormalZ=1 AngleXU=0 Radius=1
    g18: BSplineCurve PolesCount=3 KnotsCount=2 Degree=2 IsPeriodic=0
    g19: GeomPoint X=-6.2215 Y=-2 Z=0
    g20: GeomPoint X=-6.32538 Y=-4 Z=0
    g21: Circle CenterX=-6.48644 CenterY=-5.99526 CenterZ=0 NormalX=0 NormalY=0 NormalZ=1 AngleXU=0 Radius=1
    g22: Circle CenterX=-6.58486 CenterY=-6.99526 CenterZ=0 NormalX=0 NormalY=0 NormalZ=1 AngleXU=0 Radius=1
    g23: Circle CenterX=-6.77343 CenterY=-8 CenterZ=0 NormalX=0 NormalY=0 NormalZ=1 AngleXU=0 Radius=1
    g24: BSplineCurve PolesCount=3 KnotsCount=2 Degree=2 IsPeriodic=0
    g25: GeomPoint X=-6.48644 Y=-5.99526 Z=0
    g26: GeomPoint X=-6.77343 Y=-8 Z=0
    g27: Circle CenterX=-7.19003 CenterY=-10 CenterZ=0 NormalX=0 NormalY=0 NormalZ=1 AngleXU=0 Radius=1
    g28: Circle CenterX=-7.44407 CenterY=-11.0915 CenterZ=0 NormalX=0 NormalY=0 NormalZ=1 AngleXU=0 Radius=1
    g29: Circle CenterX=-7.79258 CenterY=-12 CenterZ=0 NormalX=0 NormalY=0 NormalZ=1 AngleXU=0 Radius=1
    g30: BSplineCurve PolesCount=3 KnotsCount=2 Degree=2 IsPeriodic=0
    g31: GeomPoint X=-7.19003 Y=-10 Z=0
    g32: GeomPoint X=-7.79258 Y=-12 Z=0
    g33: Circle CenterX=-8.70761 CenterY=-14 CenterZ=0 NormalX=0 NormalY=0 NormalZ=1 AngleXU=0 Radius=1
    g34: Circle CenterX=-9.33087 CenterY=-15.1837 CenterZ=0 NormalX=0 NormalY=0 NormalZ=1 AngleXU=0 Radius=1
    g35: Circle CenterX=-10.1571 CenterY=-16 CenterZ=0 NormalX=0 NormalY=0 NormalZ=1 AngleXU=0 Radius=1
    g36: BSplineCurve PolesCount=3 KnotsCount=2 Degree=2 IsPeriodic=0
    g37: GeomPoint X=-8.70761 Y=-14 Z=0
    g38: GeomPoint X=-10.1571 Y=-16 Z=0
    g39: Circle CenterX=-12.8401 CenterY=-17.6958 CenterZ=0 NormalX=0 NormalY=0 NormalZ=1 AngleXU=0 Radius=1
    g40: Circle CenterX=-13.3521 CenterY=-17.9027 CenterZ=0 NormalX=0 NormalY=0 NormalZ=1 AngleXU=0 Radius=1
    g41: Circle CenterX=-14 CenterY=-18 CenterZ=0 NormalX=0 NormalY=0 NormalZ=1 AngleXU=0 Radius=1
    g42: BSplineCurve PolesCount=3 KnotsCount=2 Degree=2 IsPeriodic=0
    g43: GeomPoint X=-12.8401 Y=-17.6958 Z=0
    g44: GeomPoint X=-14 Y=-18 Z=0
    g45: LineSegment StartX=-6.2 StartY=0 StartZ=0 EndX=-7.2 EndY=0 EndZ=0
    g46: LineSegment StartX=-7.2 StartY=0 StartZ=0 EndX=-7.2 EndY=-2 EndZ=0
    g47: LineSegment StartX=-7.2 StartY=-2 StartZ=0 EndX=-6.2215 EndY=-2 EndZ=0
    g48: LineSegment StartX=-6.32538 StartY=-4 StartZ=0 EndX=-7.65538 EndY=-4 EndZ=0
    g49: LineSegment StartX=-7.65538 StartY=-4 StartZ=0 EndX=-7.65538 EndY=-5.99526 EndZ=0
    g50: LineSegment StartX=-7.65538 StartY=-5.99526 StartZ=0 EndX=-6.48644 EndY=-5.99526 EndZ=0
    g51: LineSegment StartX=-6.77343 StartY=-8 StartZ=0 EndX=-8.43343 EndY=-8 EndZ=0
    g52: LineSegment StartX=-8.43343 StartY=-8 StartZ=0 EndX=-8.43343 EndY=-10 EndZ=0
    g53: LineSegment StartX=-8.43343 StartY=-10 StartZ=0 EndX=-7.19003 EndY=-10 EndZ=0
  constraints (112):
    c: Horizontal(g0)
    c: Distance(g0) = 2
    c: Block(g0)
    c: Vertical(g1)
    c: Coincident(g2,g0)
    c: Vertical(g2)
    c: Block(g2)
    c: Coincident(g6,g2)
    c: Weight(g3) = 1
    c: Equal(g3,g4)
    c: Equal(g3,g5)
    c: InternalAlignment(g3,g6)
    c: InternalAlignment(g4,g6)
    c: InternalAlignment(g5,g6)
    c: InternalAlignment(g7,g6)
    c: InternalAlignment(g8,g6)
    c: Block(g6)
    c: Coincident(g9,g1)
    c: Coincident(g9,g6)
    c: Horizontal(g9)
    c: Vertical(g10)
    c: Block(g10)
    c: Horizontal(g11)
    c: Block(g11)
    c: Coincident(g12,g10)
    c: Horizontal(g12)
    c: Block(g12)
    c: Coincident(g13,g11)
    c: Vertical(g13)
    c: Block(g13)
    c: Coincident(g14,g10)
    c: Horizontal(g14)
    c: Block(g14)
    c: Block(g9)
    c: Block(g1)
    c: Weight(g15) = 1
    c: Equal(g15,g16)
    c: Equal(g15,g17)
    c: InternalAlignment(g15,g18)
    c: InternalAlignment(g16,g18)
    c: InternalAlignment(g17,g18)
    c: InternalAlignment(g19,g18)
    c: InternalAlignment(g20,g18)
    c: Weight(g21) = 1
    c: Equal(g21,g22)
    c: Equal(g21,g23)
    c: InternalAlignment(g21,g24)
    c: InternalAlignment(g22,g24)
    c: InternalAlignment(g23,g24)
    c: InternalAlignment(g25,g24)
    c: InternalAlignment(g26,g24)
    c: Weight(g27) = 1
    c: Equal(g27,g28)
    c: Equal(g27,g29)
    c: Coincident(g30,g14)
    c: InternalAlignment(g27,g30)
    c: InternalAlignment(g28,g30)
    c: InternalAlignment(g29,g30)
    c: InternalAlignment(g31,g30)
    c: InternalAlignment(g32,g30)
    c: Coincident(g36,g12)
    c: Weight(g33) = 1
    c: Equal(g33,g34)
    c: Equal(g33,g35)
    c: Coincident(g36,g11)
    c: InternalAlignment(g33,g36)
    c: InternalAlignment(g34,g36)
    c: InternalAlignment(g35,g36)
    c: InternalAlignment(g37,g36)
    c: InternalAlignment(g38,g36)
    c: Coincident(g42,g13)
    c: Weight(g39) = 1
    c: Equal(g39,g40)
    c: Equal(g39,g41)
    c: Coincident(g42,g1)
    c: InternalAlignment(g39,g42)
    c: InternalAlignment(g40,g42)
    c: InternalAlignment(g41,g42)
    c: InternalAlignment(g43,g42)
    c: InternalAlignment(g44,g42)
    c: Block(g18)
    c: Block(g24)
    c: Block(g30)
    c: Block(g36)
    c: Block(g42)
    c: Horizontal(g45)
    c: Coincident(g45,g0)
    c: Vertical(g46)
    c: Coincident(g46,g45)
    c: Coincident(g47,g46)
    c: Coincident(g47,g18)
    c: Horizontal(g47)
    c: Block(g46)
    c: Coincident(g48,g18)
    c: Horizontal(g48)
    c: Distance(g48) = 1.33
    c: Vertical(g49)
    c: Coincident(g49,g48)
    c: Coincident(g50,g49)
    c: Coincident(g50,g24)
    c: Horizontal(g50)
    c: Tangent(g50,g22)
    c: Horizontal(g51)
    c: Coincident(g51,g24)
    c: Block(g51)
    c: Vertical(g52)
    c: Block(g52)
    c: Coincident(g52,g51)
    c: Coincident(g53,g52)
    c: Coincident(g53,g30)
    c: Horizontal(g53)
    c: Distance(g1) = 8.5
FEATURE [Part::Feature] Face024
  shape: bbox 9.8 x 26.5 x 2e-07 mm, 1 faces, 0 solids (baked)
FEATURE [Part::Revolution] Revolve024
  Angle = 360
  Axis = (0,1,0)
  Base = (0,0,0)
  FaceMakerClass = Part::FaceMakerBullseye
  Placement = pos=(0,0,0) rot=(0,0,1;1.5708rad)
  Solid = false
  Source = -> Face024
  Symmetric = false
FEATURE [Part::Feature] Face025
  shape: bbox 9.8 x 26.5 x 2e-07 mm, 1 faces, 0 solids (baked)
FEATURE [Part::Revolution] Revolve025
  Angle = 360
  Axis = (0,1,0)
  Base = (0,0,0)
  FaceMakerClass = Part::FaceMakerBullseye
  Placement = pos=(0,0,0) rot=(0,0,1;1.5708rad)
  Solid = false
  Source = -> Face025
  Symmetric = false
FEATURE [Part::MultiFuse] Fusion033
  Placement = pos=(-18,19,36) rot=(0,0,1;0rad)
  Shapes = -> [Revolve025,Revolve024]
FEATURE [Part::Cylinder] Cylinder014
  Angle = 360
  AttacherType = Attacher::AttachEngine3D
  Height = 20
  Placement = pos=(0,0,36.15) rot=(0,0,1;0rad)
  Radius = 14.3
FEATURE [Part::Cylinder] Cylinder015
  Angle = 360
  AttacherType = Attacher::AttachEngine3D
  Height = 10
  Placement = pos=(0,0,36.15) rot=(0,0,1;0rad)
  Radius = 4
FEATURE [Part::MultiFuse] Fusion034  label="removeToCreteHoleForPlugHousing004"
  Placement = pos=(-42,19,36) rot=(0,1,0;1.5708rad)
  Shapes = -> [Cylinder014,Cylinder015]
FEATURE [Part::Cut] Cut008  label="top004"
  Base = -> Cut004
  Placement = pos=(-1,0,0) rot=(0,0,1;0rad)
  Tool = -> Fusion034
FEATURE [Part::Box] Box005  label="Cube005"
  AttacherType = Attacher::AttachEngine3D
  Height = 28
  Length = 3
  Placement = pos=(110.7,19,22) rot=(0,0,1;0rad)
  Width = 15.7
FEATURE [Part::Cylinder] Cylinder016
  Angle = 360
  AttacherType = Attacher::AttachEngine3D
  Height = 10
  Placement = pos=(0,0,36.15) rot=(0,0,1;0rad)
  Radius = 4
FEATURE [Part::Cylinder] Cylinder017
  Angle = 360
  AttacherType = Attacher::AttachEngine3D
  Height = 20
  Placement = pos=(0,0,36.15) rot=(0,0,1;0rad)
  Radius = 10.3
FEATURE [Part::MultiFuse] Fusion035  label="removeToCreteHoleForPlugHousing005"
  Placement = pos=(70,19,36) rot=(0,1,0;1.5708rad)
  Shapes = -> [Cylinder017,Cylinder016]
FEATURE [Part::Cut] Cut009  label="plugHousingTab001"
  Base = -> Box005
  Placement = pos=(-107.4,-14,0) rot=(0,0,1;0rad)
  Tool = -> Fusion035
FEATURE [Part::Box] Box006  label="Cube006"
  AttacherType = Attacher::AttachEngine3D
  Height = 28
  Length = 3
  Placement = pos=(110.7,19,22) rot=(0,0,1;0rad)
  Width = 15.7
FEATURE [Part::Cylinder] Cylinder018
  Angle = 360
  AttacherType = Attacher::AttachEngine3D
  Height = 10
  Placement = pos=(0,0,36.15) rot=(0,0,1;0rad)
  Radius = 4
FEATURE [Part::Cylinder] Cylinder019
  Angle = 360
  AttacherType = Attacher::AttachEngine3D
  Height = 20
  Placement = pos=(0,0,36.15) rot=(0,0,1;0rad)
  Radius = 10.3
FEATURE [Part::MultiFuse] Fusion036  label="removeToCreteHoleForPlugHousing006"
  Placement = pos=(70,19,36) rot=(0,1,0;1.5708rad)
  Shapes = -> [Cylinder019,Cylinder018]
FEATURE [Part::Cut] Cut010  label="plugHousingTab002"
  Base = -> Box006
  Placement = pos=(-107.4,-14,0) rot=(0,0,1;0rad)
  Tool = -> Fusion036
FEATURE [Part::MultiFuse] Fusion037
  Placement = pos=(9.6,23,0) rot=(0,0,1;3.14159rad)
  Shapes = -> [Cut009,Cut010]
FEATURE [Part::Box] Box  label="Cube"
  AttacherType = Attacher::AttachEngine3D
  Height = 10
  Length = 3
  Placement = pos=(3.3,4,12) rot=(0,0,1;0rad)
  Width = 10
FEATURE [Part::Fillet] Fillet004
  Base = -> Fusion028
  Edges = 1 edges r=2: [Edge25]
FEATURE [Part::Fillet] Fillet005  label="plugHousing046"
  Base = -> Fillet004
  Edges = 1 edges r=2: [Edge8]
FEATURE [Part::Fillet] Fillet006
  Base = -> Box
  Edges = 1 edges r=2: [Edge11]
FEATURE [Part::Box] Box007  label="Cube007"
  AttacherType = Attacher::AttachEngine3D
  Height = 10
  Length = 3
  Placement = pos=(3.3,4,50) rot=(0,0,1;0rad)
  Width = 10
FEATURE [Part::Fillet] Fillet007
  Base = -> Box007
  Edges = 1 edges r=2: [Edge12]
FEATURE [Part::Box] Box008  label="Cube008"
  AttacherType = Attacher::AttachEngine3D
  Height = 28
  Length = 4
  Placement = pos=(5,0,22) rot=(0,0,1;0rad)
  Width = 10
FEATURE [Part::Fillet] Fillet008
  Base = -> Box008
  Edges = 1 edges r=1: [Edge7]
FEATURE [Part::Fillet] Fillet009
  Base = -> Fillet008
  Edges = 1 edges r=2: [Edge5]
FEATURE [Part::Fillet] Fillet010
  Base = -> Fillet009
  Edges = 1 edges r=2: [Edge2]
FEATURE [Sketcher::SketchObject] Sketch009  label="topSketch003"
  FullyConstrained = true
  sketch-geometry (4):
    g0: LineSegment StartX=16.8446 StartY=31.512 StartZ=0 EndX=16.3251 EndY=34.4666 EndZ=0
    g1: ArcOfCircle CenterX=19 CenterY=19.2524 CenterZ=0 NormalX=0 NormalY=0 NormalZ=1 AngleXU=0 Radius=15.4476 StartAngle=1.74483 EndAngle=2.72717
    g2: ArcOfCircle CenterX=19 CenterY=19.2524 CenterZ=0 NormalX=0 NormalY=0 NormalZ=1 AngleXU=0 Radius=12.4476 StartAngle=1.74483 EndAngle=2.73189
    g3: LineSegment StartX=4.86004 StartY=25.4725 StartZ=0 EndX=7.58253 EndY=24.2107 EndZ=0
  constraints (7):
    c: Block(g0)
    c: Coincident(g1,g0)
    c: Coincident(g2,g0)
    c: Coincident(g3,g1)
    c: Coincident(g3,g2)
    c: Block(g1)
    c: Block(g2)
FEATURE [Part::Extrusion] Extrude008
  Base = -> Sketch009
  Dir = (0,0,1)
  DirMode = 2
  FaceMakerClass = Part::FaceMakerBullseye
  LengthFwd = 10
  LengthRev = 0
  Placement = pos=(0,0,31) rot=(0,0,1;0rad)
  Solid = true
  Symmetric = false
FEATURE [Part::Cylinder] Cylinder020
  Angle = 360
  AttacherType = Attacher::AttachEngine3D
  Height = 20
  Placement = pos=(0,0,36.15) rot=(0,0,1;0rad)
  Radius = 8.2
FEATURE [Part::Cylinder] Cylinder021
  Angle = 360
  AttacherType = Attacher::AttachEngine3D
  Height = 10
  Placement = pos=(0,0,36.15) rot=(0,0,1;0rad)
  Radius = 4
FEATURE [Part::MultiFuse] Fusion038  label="removeToCreteHoleForPlugHousing007"
  Placement = pos=(-42,19,36) rot=(0,1,0;1.5708rad)
  Shapes = -> [Cylinder020,Cylinder021]
FEATURE [Part::Cut] Cut011
  Base = -> Extrude008
  Tool = -> Fusion038
FEATURE [Part::Fillet] Fillet011
  Base = -> Cut011
  Edges = 1 edges r=2: [Edge1]
FEATURE [Part::Fillet] Fillet012
  Base = -> Fillet011
  Edges = 1 edges r=2.5: [Edge1]
FEATURE [Part::Fillet] Fillet013
  Base = -> Fillet012
  Edges = 1 edges r=2.5: [Edge2]
FEATURE [Part::Box] Box010  label="Cube010"
  AttacherType = Attacher::AttachEngine3D
  Height = 16
  Length = 8
  Placement = pos=(12.7,31.52,28) rot=(0,0,1;0rad)
  Width = 4
FEATURE [Sketcher::SketchObject] Sketch010  label="topSketch004"
  FullyConstrained = true
  sketch-geometry (4):
    g0: LineSegment StartX=16.8446 StartY=31.512 StartZ=0 EndX=16.3251 EndY=34.4666 EndZ=0
    g1: ArcOfCircle CenterX=19 CenterY=19.2524 CenterZ=0 NormalX=0 NormalY=0 NormalZ=1 AngleXU=0 Radius=15.4476 StartAngle=1.74483 EndAngle=2.72717
    g2: ArcOfCircle CenterX=19 CenterY=19.2524 CenterZ=0 NormalX=0 NormalY=0 NormalZ=1 AngleXU=0 Radius=12.4476 StartAngle=1.74483 EndAngle=2.73189
    g3: LineSegment StartX=4.86004 StartY=25.4725 StartZ=0 EndX=7.58253 EndY=24.2107 EndZ=0
  constraints (7):
    c: Block(g0)
    c: Coincident(g1,g0)
    c: Coincident(g2,g0)
    c: Coincident(g3,g1)
    c: Coincident(g3,g2)
    c: Block(g1)
    c: Block(g2)
FEATURE [Part::Cylinder] Cylinder022
  Angle = 360
  AttacherType = Attacher::AttachEngine3D
  Height = 10
  Placement = pos=(0,0,36.15) rot=(0,0,1;0rad)
  Radius = 4
FEATURE [Sketcher::SketchObject] Sketch011  label="topSketch005"
  FullyConstrained = true
  sketch-geometry (4):
    g0: LineSegment StartX=16.8446 StartY=31.512 StartZ=0 EndX=16.3251 EndY=34.4666 EndZ=0
    g1: ArcOfCircle CenterX=19 CenterY=19.2524 CenterZ=0 NormalX=0 NormalY=0 NormalZ=1 AngleXU=0 Radius=15.4476 StartAngle=1.74483 EndAngle=2.72717
    g2: ArcOfCircle CenterX=19 CenterY=19.2524 CenterZ=0 NormalX=0 NormalY=0 NormalZ=1 AngleXU=0 Radius=12.4476 StartAngle=1.74483 EndAngle=2.73189
    g3: LineSegment StartX=4.86004 StartY=25.4725 StartZ=0 EndX=7.58253 EndY=24.2107 EndZ=0
  constraints (7):
    c: Block(g0)
    c: Coincident(g1,g0)
    c: Coincident(g2,g0)
    c: Coincident(g3,g1)
    c: Coincident(g3,g2)
    c: Block(g1)
    c: Block(g2)
FEATURE [Part::Extrusion] Extrude010
  Base = -> Sketch011
  Dir = (0,0,1)
  DirMode = 2
  FaceMakerClass = Part::FaceMakerBullseye
  LengthFwd = 10.6
  LengthRev = 0
  Placement = pos=(0,0,31) rot=(0,0,1;0rad)
  Solid = true
  Symmetric = false
FEATURE [Part::Cylinder] Cylinder023
  Angle = 360
  AttacherType = Attacher::AttachEngine3D
  Height = 20
  Placement = pos=(0,0,36.15) rot=(0,0,1;0rad)
  Radius = 8.2
FEATURE [Part::MultiFuse] Fusion039  label="removeToCreteHoleForPlugHousing008"
  Placement = pos=(-42,19,36) rot=(0,1,0;1.5708rad)
  Shapes = -> [Cylinder023,Cylinder022]
FEATURE [Part::Cut] Cut012
  Base = -> Extrude010
  Placement = pos=(0,0,-0.3) rot=(0,0,1;0rad)
  Tool = -> Fusion039
FEATURE [Part::Cut] Cut013
  Base = -> Box010
  Tool = -> Cut012
FEATURE [Part::Fillet] Fillet014
  Base = -> Cut013
  Edges = 1 edges r=0.7: [Edge13]
FEATURE [Part::Fillet] Fillet015
  Base = -> Fillet014
  Edges = 1 edges r=0.7: [Edge13]
FEATURE [Part::Fillet] Fillet016
  Base = -> Fillet015
  Edges = 1 edges r=0.7: [Edge16]
FEATURE [Part::Fillet] Fillet017
  Base = -> Fillet016
  Edges = 1 edges r=0.7: [Edge11]
FEATURE [Part::Fillet] Fillet018
  Base = -> Fillet017
  Edges = 1 edges r=0.7: [Edge10]
FEATURE [Part::Fillet] Fillet019
  Base = -> Fillet018
  Edges = 1 edges r=1.2: [Edge5]
FEATURE [Part::Fillet] Fillet020
  Base = -> Fillet019
  Edges = 1 edges r=1.2: [Edge12]
FEATURE [Part::Fillet] Fillet021
  Base = -> Fillet020
  Edges = 1 edges r=2: [Edge1]
  Placement = pos=(0.3,0,0) rot=(0,0,1;0rad)
FEATURE [Part::MultiFuse] Fusion040  label="top005"
  Shapes = -> [Cut008,Fillet021]
FEATURE [Part::MultiFuse] Fusion041  label="wireHolder"
  Shapes = -> [Fusion033,Fillet013]
FEATURE [Part::MultiFuse] Fusion042
  Shapes = -> [Fillet007,Fusion041]
FEATURE [Part::MultiFuse] Fusion043  label="wireHolder001"
  Shapes = -> [Fusion042,Fillet010]
FEATURE [Part::MultiFuse] Fusion044  label="wireHolder002"
  Shapes = -> [Fillet006,Fusion037,Fusion043]
FEATURE [Part::Feature] Face026
  shape: bbox 11 x 6 x 2e-07 mm, 1 faces, 0 solids (baked)
FEATURE [Part::Revolution] Revolve026
  Angle = 360
  Axis = (0,1,0)
  Base = (0,0,0)
  FaceMakerClass = Part::FaceMakerBullseye
  Placement = pos=(30.3,-1,19.7) rot=(0,0,1;0rad)
  Solid = false
  Source = -> Face026
  Symmetric = false
FEATURE [Sketcher::SketchObject] Sketch013  label="topSketch006"
  FullyConstrained = true
  sketch-geometry (13):
    g0: LineSegment StartX=117 StartY=19 StartZ=0 EndX=117 EndY=38 EndZ=0
    g1: ArcOfCircle CenterX=98 CenterY=19 CenterZ=0 NormalX=0 NormalY=0 NormalZ=1 AngleXU=0 Radius=19 StartAngle=5.7297 EndAngle=6.28319
    g2: LineSegment StartX=0 StartY=3 StartZ=0 EndX=0 EndY=19 EndZ=0
    g3: LineSegment StartX=19 StartY=38 StartZ=0 EndX=117 EndY=38 EndZ=0
    g4: ArcOfCircle CenterX=19 CenterY=19 CenterZ=0 NormalX=0 NormalY=0 NormalZ=1 AngleXU=0 Radius=19 StartAngle=1.5708 EndAngle=3.14159
    g5: ArcOfCircle CenterX=19 CenterY=19 CenterZ=0 NormalX=0 NormalY=0 NormalZ=1 AngleXU=0 Radius=16 StartAngle=1.5708 EndAngle=3.14159
    g6: ArcOfCircle CenterX=98 CenterY=19 CenterZ=0 NormalX=0 NormalY=0 NormalZ=1 AngleXU=0 Radius=16 StartAngle=5.60905 EndAngle=6.28319
    g7: LineSegment StartX=114 StartY=19 StartZ=0 EndX=114 EndY=35 EndZ=0
    g8: LineSegment StartX=110.5 StartY=9.01251 StartZ=0 EndX=114.163 EndY=9.01251 EndZ=0
    g9: LineSegment StartX=114 StartY=35 StartZ=0 EndX=19 EndY=35 EndZ=0
    g10: LineSegment StartX=0 StartY=3 StartZ=0 EndX=0 EndY=0 EndZ=0
    g11: LineSegment StartX=3 StartY=0 StartZ=0 EndX=0 EndY=0 EndZ=0
    g12: LineSegment StartX=3 StartY=19 StartZ=0 EndX=3 EndY=0 EndZ=0
  constraints (33):
    c: Vertical(g0)
    c: Distance(g0) = 19
    c: Block(g0)
    c: Coincident(g1,g0)
    c: Block(g1)
    c: Vertical(g2)
    c: Block(g2)
    c: Coincident(g3,g0)
    c: Horizontal(g3)
    c: Distance(g3) = 98
    c: Coincident(g4,g3)
    c: Coincident(g4,g2)
    c: Block(g4)
    c: Coincident(g5,g4)
    c: Coincident(g6,g1)
    c: Block(g6)
    c: Block(g5)
    c: Coincident(g7,g6)
    c: Vertical(g7)
    c: Coincident(g8,g6)
    c: Coincident(g8,g1)
    c: Coincident(g9,g7)
    c: Coincident(g9,g5)
    c: Horizontal(g9)
    c: Tangent(g9,g5)
    c: Coincident(g10,g2)
    c: Distance(g10) = 3
    c: Vertical(g10)
    c: Coincident(g11,g10)
    c: Horizontal(g11)
    c: Coincident(g12,g5)
    c: Coincident(g12,g11)
    c: Vertical(g12)
FEATURE [Part::Extrusion] Extrude011  label="top006"
  Base = -> Sketch013
  Dir = (0,0,1)
  DirMode = 2
  FaceMakerClass = Part::FaceMakerBullseye
  LengthFwd = 72
  LengthRev = 0
  Solid = true
  Symmetric = false
FEATURE [Sketcher::SketchObject] Sketch014
  FullyConstrained = true
  MapMode = 3
  Placement = pos=(0,0,0) rot=(1,0,0;1.5708rad)
  Support = -> [Extrude011]
  sketch-geometry (8):
    g0: Circle CenterX=80.351 CenterY=-67.6202 CenterZ=0 NormalX=0 NormalY=0 NormalZ=1 AngleXU=0 Radius=2
    g1: Circle CenterX=80.351 CenterY=-67.6202 CenterZ=0 NormalX=0 NormalY=0 NormalZ=1 AngleXU=0 Radius=3
    g2: Circle CenterX=80.351 CenterY=-4.92017 CenterZ=0 NormalX=0 NormalY=0 NormalZ=1 AngleXU=0 Radius=2
    g3: Circle CenterX=80.351 CenterY=-4.92017 CenterZ=0 NormalX=0 NormalY=0 NormalZ=1 AngleXU=0 Radius=3
    g4: Circle CenterX=23.851 CenterY=-4.92017 CenterZ=0 NormalX=0 NormalY=0 NormalZ=1 AngleXU=0 Radius=2
    g5: Circle CenterX=23.851 CenterY=-4.92017 CenterZ=0 NormalX=0 NormalY=0 NormalZ=1 AngleXU=0 Radius=3
    g6: Circle CenterX=23.851 CenterY=-67.6202 CenterZ=0 NormalX=0 NormalY=0 NormalZ=1 AngleXU=0 Radius=2
    g7: Circle CenterX=23.851 CenterY=-67.6202 CenterZ=0 NormalX=0 NormalY=0 NormalZ=1 AngleXU=0 Radius=3
  constraints (8):
    c: Block(g3)
    c: Block(g2)
    c: Block(g1)
    c: Block(g0)
    c: Block(g6)
    c: Block(g7)
    c: Block(g4)
    c: Block(g5)
FEATURE [Part::Feature] Face027
  shape: bbox 11 x 6 x 2e-07 mm, 1 faces, 0 solids (baked)
FEATURE [Part::Revolution] Revolve027
  Angle = 360
  Axis = (0,1,0)
  Base = (0,0,0)
  FaceMakerClass = Part::FaceMakerBullseye
  Placement = pos=(30.3,-1,51.7) rot=(0,0,1;0rad)
  Solid = false
  Source = -> Face027
  Symmetric = false
FEATURE [Part::Feature] Face028
  shape: bbox 11 x 6 x 2e-07 mm, 1 faces, 0 solids (baked)
FEATURE [Part::Revolution] Revolve028
  Angle = 360
  Axis = (0,1,0)
  Base = (0,0,0)
  FaceMakerClass = Part::FaceMakerBullseye
  Placement = pos=(62.3,-1,19.7) rot=(0,0,1;0rad)
  Solid = false
  Source = -> Face028
  Symmetric = false
FEATURE [Part::Feature] Face029
  shape: bbox 11 x 6 x 2e-07 mm, 1 faces, 0 solids (baked)
FEATURE [Part::Revolution] Revolve029
  Angle = 360
  Axis = (0,1,0)
  Base = (0,0,0)
  FaceMakerClass = Part::FaceMakerBullseye
  Placement = pos=(62.3,-1,51.7) rot=(0,0,1;0rad)
  Solid = false
  Source = -> Face029
  Symmetric = false
FEATURE [Part::Feature] Wire
  shape: bbox 11 x 5.2 x 2e-07 mm, 0 faces, 0 solids (baked)
FEATURE [Part::Revolution] Revolve030
  Angle = 360
  Axis = (0,1,0)
  Base = (0,0,0)
  FaceMakerClass = Part::FaceMakerBullseye
  Placement = pos=(30.3,38,19.7) rot=(0,0,1;0rad)
  Solid = true
  Source = -> Wire
  Symmetric = false
FEATURE [Part::Feature] Wire001
  shape: bbox 11 x 5.2 x 2e-07 mm, 0 faces, 0 solids (baked)
FEATURE [Part::Revolution] Revolve031
  Angle = 360
  Axis = (0,1,0)
  Base = (0,0,0)
  FaceMakerClass = Part::FaceMakerBullseye
  Placement = pos=(30.3,38,51.7) rot=(0,0,1;0rad)
  Solid = true
  Source = -> Wire001
  Symmetric = false
FEATURE [Part::Feature] Wire002
  shape: bbox 11 x 5.2 x 2e-07 mm, 0 faces, 0 solids (baked)
FEATURE [Part::Revolution] Revolve032
  Angle = 360
  Axis = (0,1,0)
  Base = (0,0,0)
  FaceMakerClass = Part::FaceMakerBullseye
  Placement = pos=(62.3,38,51.7) rot=(0,0,1;0rad)
  Solid = true
  Source = -> Wire002
  Symmetric = false
FEATURE [Part::Feature] Wire003
  shape: bbox 11 x 5.2 x 2e-07 mm, 0 faces, 0 solids (baked)
FEATURE [Part::Revolution] Revolve033
  Angle = 360
  Axis = (0,1,0)
  Base = (0,0,0)
  FaceMakerClass = Part::FaceMakerBullseye
  Placement = pos=(62.3,38,19.7) rot=(0,0,1;0rad)
  Solid = true
  Source = -> Wire003
  Symmetric = false
FEATURE [Part::MultiFuse] Fusion045  label="altRandScrewHousing"
  Shapes = -> [Revolve029,Revolve027,Revolve028,Revolve026]
FEATURE [Part::MultiFuse] Fusion046  label="fanScrewHousing"
  Shapes = -> [Revolve033,Revolve032,Revolve031,Revolve030]
FEATURE [Sketcher::SketchObject] Sketch015
  FullyConstrained = true
  sketch-geometry (17):
    g0: Circle CenterX=-3.5 CenterY=23.5 CenterZ=0 NormalX=0 NormalY=0 NormalZ=1 AngleXU=0 Radius=1
    g1: Circle CenterX=-1 CenterY=15.25 CenterZ=0 NormalX=0 NormalY=0 NormalZ=1 AngleXU=0 Radius=1
    g2: Circle CenterX=-3.5 CenterY=7 CenterZ=0 NormalX=0 NormalY=0 NormalZ=1 AngleXU=0 Radius=1
    g3: BSplineCurve PolesCount=3 KnotsCount=2 Degree=2 IsPeriodic=0
    g4: GeomPoint X=-3.5 Y=23.5 Z=0
    g5: GeomPoint X=-3.5 Y=7 Z=0
    g6: Circle CenterX=-4.8 CenterY=30.5 CenterZ=0 NormalX=0 NormalY=0 NormalZ=1 AngleXU=0 Radius=1
    g7: Circle CenterX=-3.5 CenterY=30.5 CenterZ=0 NormalX=0 NormalY=0 NormalZ=1 AngleXU=0 Radius=1
    g8: Circle CenterX=-3.5 CenterY=29.2 CenterZ=0 NormalX=0 NormalY=0 NormalZ=1 AngleXU=0 Radius=1
    g9: BSplineCurve PolesCount=3 KnotsCount=2 Degree=2 IsPeriodic=0
    g10: GeomPoint X=-4.8 Y=30.5 Z=0
    g11: GeomPoint X=-3.5 Y=29.2 Z=0
    g12: LineSegment StartX=-3.5 StartY=29.2 StartZ=0 EndX=-3.5 EndY=23.5 EndZ=0
    g13: LineSegment StartX=-4.8 StartY=30.5 StartZ=0 EndX=0 EndY=30.5 EndZ=0
    g14: LineSegment StartX=-3.5 StartY=0.3 StartZ=0 EndX=0 EndY=0.3 EndZ=0
    g15: LineSegment StartX=-3.5 StartY=0.3 StartZ=0 EndX=-3.5 EndY=7 EndZ=0
    g16: LineSegment StartX=0 StartY=0.3 StartZ=0 EndX=0 EndY=30.5 EndZ=0
  constraints (33):
    c: Weight(g0) = 1
    c: Equal(g0,g1)
    c: Equal(g0,g2)
    c: InternalAlignment(g0,g3)
    c: InternalAlignment(g1,g3)
    c: InternalAlignment(g2,g3)
    c: InternalAlignment(g4,g3)
    c: InternalAlignment(g5,g3)
    c: Block(g3)
    c: Weight(g6) = 1
    c: Equal(g6,g7)
    c: Equal(g6,g8)
    c: InternalAlignment(g6,g9)
    c: InternalAlignment(g7,g9)
    c: InternalAlignment(g8,g9)
    c: InternalAlignment(g10,g9)
    c: InternalAlignment(g11,g9)
    c: Block(g9)
    c: Coincident(g12,g9)
    c: Coincident(g12,g3)
    c: Vertical(g12)
    c: Coincident(g13,g9)
    c: Horizontal(g13)
    c: Distance(g13) = 4.8
    c: Horizontal(g14)
    c: Block(g14)
    c: Coincident(g15,g14)
    c: Coincident(g15,g3)
    c: Vertical(g15)
    c: Coincident(g16,g14)
    c: Coincident(g16,g13)
    c: Vertical(g16)
    c: Tangent(g16,g1)
FEATURE [Sketcher::SketchObject] Sketch016
  FullyConstrained = true
  sketch-geometry (16):
    g0: Circle CenterX=-3.5 CenterY=23.5 CenterZ=0 NormalX=0 NormalY=0 NormalZ=1 AngleXU=0 Radius=1
    g1: Circle CenterX=-1 CenterY=15.25 CenterZ=0 NormalX=0 NormalY=0 NormalZ=1 AngleXU=0 Radius=1
    g2: Circle CenterX=-3.5 CenterY=7 CenterZ=0 NormalX=0 NormalY=0 NormalZ=1 AngleXU=0 Radius=1
    g3: BSplineCurve PolesCount=3 KnotsCount=2 Degree=2 IsPeriodic=0
    g4: GeomPoint X=-3.5 Y=23.5 Z=0
    g5: GeomPoint X=-3.5 Y=7 Z=0
    g6: LineSegment StartX=-3.5 StartY=28.2 StartZ=0 EndX=-3.5 EndY=23.5 EndZ=0
    g7: LineSegment StartX=0 StartY=29.5 StartZ=0 EndX=0 EndY=30 EndZ=0
    g8: LineSegment StartX=-3.5 StartY=28.2 StartZ=0 EndX=-3.5 EndY=30 EndZ=0
    g9: LineSegment StartX=0 StartY=30 StartZ=0 EndX=0 EndY=30.5 EndZ=0
    g10: LineSegment StartX=0 StartY=30.5 StartZ=0 EndX=-3.5 EndY=30.5 EndZ=0
    g11: LineSegment StartX=-3.5 StartY=30.5 StartZ=0 EndX=-3.5 EndY=30 EndZ=0
    g12: LineSegment StartX=0 StartY=29.5 StartZ=0 EndX=0 EndY=5 EndZ=0
    g13: LineSegment StartX=-3.5 StartY=0.3 StartZ=0 EndX=-3.5 EndY=7 EndZ=0
    g14: LineSegment StartX=-3.5 StartY=0.3 StartZ=0 EndX=0 EndY=0.3 EndZ=0
    g15: LineSegment StartX=0 StartY=5 StartZ=0 EndX=0 EndY=0.3 EndZ=0
  constraints (39):
    c: Weight(g0) = 1
    c: Equal(g0,g1)
    c: Equal(g0,g2)
    c: InternalAlignment(g0,g3)
    c: InternalAlignment(g1,g3)
    c: InternalAlignment(g2,g3)
    c: InternalAlignment(g4,g3)
    c: InternalAlignment(g5,g3)
    c: Block(g3)
    c: Coincident(g6,g3)
    c: Vertical(g6)
    c: Vertical(g7)
    c: Distance(g7) = 0.5
    c: Coincident(g8,g6)
    c: Vertical(g8)
    c: Block(g6)
    c: Block(g7)
    c: Vertical(g9)
    c: Equal(g7,g9) = 0.5
    c: Block(g9)
    c: Coincident(g9,g7)
    c: Horizontal(g10)
    c: Coincident(g10,g9)
    c: Coincident(g11,g10)
    c: Coincident(g11,g8)
    c: Vertical(g11)
    c: Block(g11)
    c: Coincident(g12,g7)
    c: Vertical(g12)
    c: Coincident(g13,g3)
    c: Vertical(g13)
    c: Distance(g13) = 6.7
    c: Coincident(g14,g13)
    c: Horizontal(g14)
    c: Block(g14)
    c: Coincident(g15,g12)
    c: Coincident(g15,g14)
    c: Vertical(g15)
    c: Block(g15)
FEATURE [Sketcher::SketchObject] Sketch017
  FullyConstrained = true
  sketch-geometry (11):
    g0: LineSegment StartX=-3.5 StartY=1e-16 StartZ=0 EndX=-1.6 EndY=1e-16 EndZ=0
    g1: LineSegment StartX=-1.6 StartY=1e-16 StartZ=0 EndX=-1.6 EndY=1.5 EndZ=0
    g2: LineSegment StartX=-3.5 StartY=1.5 StartZ=0 EndX=-1.6 EndY=1.5 EndZ=0
    g3: LineSegment StartX=-3.5 StartY=1e-16 StartZ=0 EndX=-4.8 EndY=1e-16 EndZ=0
    g4: Circle CenterX=-3.5 CenterY=1.3 CenterZ=0 NormalX=0 NormalY=0 NormalZ=1 AngleXU=0 Radius=1
    g5: Circle CenterX=-3.5 CenterY=1e-16 CenterZ=0 NormalX=0 NormalY=0 NormalZ=1 AngleXU=0 Radius=1
    g6: Circle CenterX=-4.8 CenterY=1e-16 CenterZ=0 NormalX=0 NormalY=0 NormalZ=1 AngleXU=0 Radius=1
    g7: BSplineCurve PolesCount=3 KnotsCount=2 Degree=2 IsPeriodic=0
    g8: GeomPoint X=-3.5 Y=1.3 Z=0
    g9: GeomPoint X=-4.8 Y=1e-16 Z=0
    g10: LineSegment StartX=-3.5 StartY=1.3 StartZ=0 EndX=-3.5 EndY=1.5 EndZ=0
  constraints (24):
    c: Horizontal(g0)
    c: Distance(g0) = 1.9
    c: Block(g0)
    c: Coincident(g1,g0)
    c: Vertical(g1)
    c: Coincident(g2,g1)
    c: Horizontal(g2)
    c: Coincident(g3,g0)
    c: Horizontal(g3)
    c: Distance(g3) = 1.3
    c: Weight(g4) = 1
    c: Equal(g4,g5)
    c: Coincident(g5,g0)
    c: Equal(g4,g6)
    c: Coincident(g7,g3)
    c: InternalAlignment(g4,g7)
    c: InternalAlignment(g5,g7)
    c: InternalAlignment(g6,g7)
    c: InternalAlignment(g8,g7)
    c: InternalAlignment(g9,g7)
    c: Coincident(g10,g7)
    c: Coincident(g10,g2)
    c: Vertical(g10)
    c: Block(g10)
FEATURE [Part::Feature] Face035
  shape: bbox 3.2 x 1.5 x 2e-07 mm, 1 faces, 0 solids (baked)
FEATURE [Part::Revolution] Revolve039  label="backCaseScrewRetainer"
  Angle = 360
  Axis = (0,1,0)
  Base = (0,0,0)
  FaceMakerClass = Part::FaceMakerBullseye
  Placement = pos=(12.5,3,62) rot=(0,0,1;0rad)
  Solid = false
  Source = -> Face035
  Symmetric = false
FEATURE [Part::Feature] Face036
  shape: bbox 3.2 x 1.5 x 2e-07 mm, 1 faces, 0 solids (baked)
FEATURE [Part::Feature] Face039
  shape: bbox 4.8 x 30.2 x 2e-07 mm, 1 faces, 0 solids (baked)
FEATURE [Part::Revolution] Revolve043  label="frontCaseScrewPost002"
  Angle = 360
  Axis = (0,1,0)
  Base = (0,0,0)
  FaceMakerClass = Part::FaceMakerBullseye
  Placement = pos=(89.5,4.5,3.5) rot=(0,0,1;0rad)
  Solid = false
  Source = -> Face039
  Symmetric = false
FEATURE [Part::Feature] Face042
  shape: bbox 4.8 x 30.2 x 2e-07 mm, 1 faces, 0 solids (baked)
FEATURE [Part::Revolution] Revolve046  label="frontCaseScrewPost003"
  Angle = 360
  Axis = (0,1,0)
  Base = (0,0,0)
  FaceMakerClass = Part::FaceMakerBullseye
  Placement = pos=(89.5,4.5,68.5) rot=(0,0,1;0rad)
  Solid = false
  Source = -> Face042
  Symmetric = false
FEATURE [Part::Feature] Face043
  shape: bbox 3.2 x 1.5 x 2e-07 mm, 1 faces, 0 solids (baked)
FEATURE [Part::Revolution] Revolve047  label="frontCaseScrewRetainer002"
  Angle = 360
  Axis = (0,1,0)
  Base = (0,0,0)
  FaceMakerClass = Part::FaceMakerBullseye
  Placement = pos=(89.5,3,68.5) rot=(0,0,1;0rad)
  Solid = false
  Source = -> Face043
  Symmetric = false
FEATURE [Part::Feature] Face044
  shape: bbox 3.2 x 1.5 x 2e-07 mm, 1 faces, 0 solids (baked)
FEATURE [Part::Revolution] Revolve048  label="frontCaseScrewRetainer003"
  Angle = 360
  Axis = (0,1,0)
  Base = (0,0,0)
  FaceMakerClass = Part::FaceMakerBullseye
  Placement = pos=(89.5,3,3.5) rot=(0,0,1;0rad)
  Solid = false
  Source = -> Face044
  Symmetric = false
FEATURE [App::MeasureDistance] Distance002  label="Distance: 1.67 mm"
  Distance = 1.66921
  P1 = (99.2361,4.7524,71.7)
  P2 = (99.2347,6.42161,71.7)
FEATURE [Sketcher::SketchObject] Sketch018
  FullyConstrained = true
  sketch-geometry (7):
    g0: LineSegment StartX=0 StartY=0 StartZ=0 EndX=0 EndY=6 EndZ=0
    g1: Circle CenterX=0 CenterY=0 CenterZ=0 NormalX=0 NormalY=0 NormalZ=1 AngleXU=0 Radius=1
    g2: Circle CenterX=8 CenterY=6 CenterZ=0 NormalX=0 NormalY=0 NormalZ=1 AngleXU=0 Radius=1
    g3: BSplineCurve PolesCount=3 KnotsCount=2 Degree=2 IsPeriodic=0
    g4: GeomPoint X=0 Y=0 Z=0
    g5: GeomPoint X=8 Y=6 Z=0
    g6: LineSegment StartX=0 StartY=6 StartZ=0 EndX=8 EndY=6 EndZ=0
  constraints (14):
    c: Coincident(g0,g-1)
    c: Distance(g0) = 6
    c: Vertical(g0)
    c: Coincident(g3,g0)
    c: Weight(g1) = 1
    c: Equal(g1,g2)
    c: InternalAlignment(g1,g3)
    c: InternalAlignment(g2,g3)
    c: InternalAlignment(g4,g3)
    c: InternalAlignment(g5,g3)
    c: Block(g3)
    c: Coincident(g6,g0)
    c: Coincident(g6,g3)
    c: Horizontal(g6)
FEATURE [Part::Extrusion] Extrude012  label="caseScrewPillarBracket"
  Base = -> Sketch018
  Dir = (0,0,1)
  DirMode = 2
  FaceMakerClass = Part::FaceMakerBullseye
  LengthFwd = 2.4
  LengthRev = 0
  Placement = pos=(15.76,29,8.8) rot=(0,1,0;0rad)
  Solid = true
  Symmetric = false
FEATURE [Sketcher::SketchObject] Sketch019
  FullyConstrained = true
  sketch-geometry (7):
    g0: LineSegment StartX=0 StartY=0 StartZ=0 EndX=0 EndY=6 EndZ=0
    g1: Circle CenterX=0 CenterY=0 CenterZ=0 NormalX=0 NormalY=0 NormalZ=1 AngleXU=0 Radius=1
    g2: Circle CenterX=8 CenterY=6 CenterZ=0 NormalX=0 NormalY=0 NormalZ=1 AngleXU=0 Radius=1
    g3: BSplineCurve PolesCount=3 KnotsCount=2 Degree=2 IsPeriodic=0
    g4: GeomPoint X=0 Y=0 Z=0
    g5: GeomPoint X=8 Y=6 Z=0
    g6: LineSegment StartX=0 StartY=6 StartZ=0 EndX=8 EndY=6 EndZ=0
  constraints (14):
    c: Coincident(g0,g-1)
    c: Distance(g0) = 6
    c: Vertical(g0)
    c: Coincident(g3,g0)
    c: Weight(g1) = 1
    c: Equal(g1,g2)
    c: InternalAlignment(g1,g3)
    c: InternalAlignment(g2,g3)
    c: InternalAlignment(g4,g3)
    c: InternalAlignment(g5,g3)
    c: Block(g3)
    c: Coincident(g6,g0)
    c: Coincident(g6,g3)
    c: Horizontal(g6)
FEATURE [Part::Extrusion] Extrude013  label="caseScrewPillarBracket001"
  Base = -> Sketch019
  Dir = (0,0,1)
  DirMode = 2
  FaceMakerClass = Part::FaceMakerBullseye
  LengthFwd = 2.4
  LengthRev = 0
  Placement = pos=(15.76,29,60.8) rot=(0,0,1;0rad)
  Solid = true
  Symmetric = false
FEATURE [Sketcher::SketchObject] Sketch020
  FullyConstrained = true
  sketch-geometry (7):
    g0: LineSegment StartX=0 StartY=0 StartZ=0 EndX=0 EndY=6 EndZ=0
    g1: Circle CenterX=0 CenterY=0 CenterZ=0 NormalX=0 NormalY=0 NormalZ=1 AngleXU=0 Radius=1
    g2: Circle CenterX=8 CenterY=6 CenterZ=0 NormalX=0 NormalY=0 NormalZ=1 AngleXU=0 Radius=1
    g3: BSplineCurve PolesCount=3 KnotsCount=2 Degree=2 IsPeriodic=0
    g4: GeomPoint X=0 Y=0 Z=0
    g5: GeomPoint X=8 Y=6 Z=0
    g6: LineSegment StartX=0 StartY=6 StartZ=0 EndX=8 EndY=6 EndZ=0
  constraints (14):
    c: Coincident(g0,g-1)
    c: Distance(g0) = 6
    c: Vertical(g0)
    c: Coincident(g3,g0)
    c: Weight(g1) = 1
    c: Equal(g1,g2)
    c: InternalAlignment(g1,g3)
    c: InternalAlignment(g2,g3)
    c: InternalAlignment(g4,g3)
    c: InternalAlignment(g5,g3)
    c: Block(g3)
    c: Coincident(g6,g0)
    c: Coincident(g6,g3)
    c: Horizontal(g6)
FEATURE [Part::Extrusion] Extrude014  label="caseScrewPillarBracket002"
  Base = -> Sketch020
  Dir = (0,0,1)
  DirMode = 2
  FaceMakerClass = Part::FaceMakerBullseye
  LengthFwd = 2.4
  LengthRev = 0
  Placement = pos=(13.7,29,13.26) rot=(0,1,0;-1.5708rad)
  Solid = true
  Symmetric = false
FEATURE [Sketcher::SketchObject] Sketch021
  FullyConstrained = true
  sketch-geometry (7):
    g0: LineSegment StartX=0 StartY=0 StartZ=0 EndX=0 EndY=6 EndZ=0
    g1: Circle CenterX=0 CenterY=0 CenterZ=0 NormalX=0 NormalY=0 NormalZ=1 AngleXU=0 Radius=1
    g2: Circle CenterX=8 CenterY=6 CenterZ=0 NormalX=0 NormalY=0 NormalZ=1 AngleXU=0 Radius=1
    g3: BSplineCurve PolesCount=3 KnotsCount=2 Degree=2 IsPeriodic=0
    g4: GeomPoint X=0 Y=0 Z=0
    g5: GeomPoint X=8 Y=6 Z=0
    g6: LineSegment StartX=0 StartY=6 StartZ=0 EndX=8 EndY=6 EndZ=0
  constraints (14):
    c: Coincident(g0,g-1)
    c: Distance(g0) = 6
    c: Vertical(g0)
    c: Coincident(g3,g0)
    c: Weight(g1) = 1
    c: Equal(g1,g2)
    c: InternalAlignment(g1,g3)
    c: InternalAlignment(g2,g3)
    c: InternalAlignment(g4,g3)
    c: InternalAlignment(g5,g3)
    c: Block(g3)
    c: Coincident(g6,g0)
    c: Coincident(g6,g3)
    c: Horizontal(g6)
FEATURE [Part::Extrusion] Extrude015  label="caseScrewPillarBracket003"
  Base = -> Sketch021
  Dir = (0,0,1)
  DirMode = 2
  FaceMakerClass = Part::FaceMakerBullseye
  LengthFwd = 2.4
  LengthRev = 0
  Placement = pos=(11.3,29,58.74) rot=(0,1,0;1.5708rad)
  Solid = true
  Symmetric = false
FEATURE [Sketcher::SketchObject] Sketch022
  FullyConstrained = true
  sketch-geometry (7):
    g0: LineSegment StartX=0 StartY=0 StartZ=0 EndX=0 EndY=6 EndZ=0
    g1: Circle CenterX=0 CenterY=0 CenterZ=0 NormalX=0 NormalY=0 NormalZ=1 AngleXU=0 Radius=1
    g2: Circle CenterX=8 CenterY=6 CenterZ=0 NormalX=0 NormalY=0 NormalZ=1 AngleXU=0 Radius=1
    g3: BSplineCurve PolesCount=3 KnotsCount=2 Degree=2 IsPeriodic=0
    g4: GeomPoint X=0 Y=0 Z=0
    g5: GeomPoint X=8 Y=6 Z=0
    g6: LineSegment StartX=0 StartY=6 StartZ=0 EndX=8 EndY=6 EndZ=0
  constraints (14):
    c: Coincident(g0,g-1)
    c: Distance(g0) = 6
    c: Vertical(g0)
    c: Coincident(g3,g0)
    c: Weight(g1) = 1
    c: Equal(g1,g2)
    c: InternalAlignment(g1,g3)
    c: InternalAlignment(g2,g3)
    c: InternalAlignment(g4,g3)
    c: InternalAlignment(g5,g3)
    c: Block(g3)
    c: Coincident(g6,g0)
    c: Coincident(g6,g3)
    c: Horizontal(g6)
FEATURE [Part::Extrusion] Extrude016  label="caseScrewPillarBracket004"
  Base = -> Sketch022
  Dir = (0,0,1)
  DirMode = 2
  FaceMakerClass = Part::FaceMakerBullseye
  LengthFwd = 2.4
  LengthRev = 0
  Placement = pos=(88.3,29,65.23) rot=(0,1,0;1.5708rad)
  Solid = true
  Symmetric = false
FEATURE [Sketcher::SketchObject] Sketch023
  FullyConstrained = true
  sketch-geometry (7):
    g0: LineSegment StartX=0 StartY=0 StartZ=0 EndX=0 EndY=6 EndZ=0
    g1: Circle CenterX=0 CenterY=0 CenterZ=0 NormalX=0 NormalY=0 NormalZ=1 AngleXU=0 Radius=1
    g2: Circle CenterX=8 CenterY=6 CenterZ=0 NormalX=0 NormalY=0 NormalZ=1 AngleXU=0 Radius=1
    g3: BSplineCurve PolesCount=3 KnotsCount=2 Degree=2 IsPeriodic=0
    g4: GeomPoint X=0 Y=0 Z=0
    g5: GeomPoint X=8 Y=6 Z=0
    g6: LineSegment StartX=0 StartY=6 StartZ=0 EndX=8 EndY=6 EndZ=0
  constraints (14):
    c: Coincident(g0,g-1)
    c: Distance(g0) = 6
    c: Vertical(g0)
    c: Coincident(g3,g0)
    c: Weight(g1) = 1
    c: Equal(g1,g2)
    c: InternalAlignment(g1,g3)
    c: InternalAlignment(g2,g3)
    c: InternalAlignment(g4,g3)
    c: InternalAlignment(g5,g3)
    c: Block(g3)
    c: Coincident(g6,g0)
    c: Coincident(g6,g3)
    c: Horizontal(g6)
FEATURE [Part::Extrusion] Extrude017  label="caseScrewPillarBracket005"
  Base = -> Sketch023
  Dir = (0,0,1)
  DirMode = 2
  FaceMakerClass = Part::FaceMakerBullseye
  LengthFwd = 2.4
  LengthRev = 0
  Placement = pos=(90.7,29,6.77) rot=(0,-1,0;1.5708rad)
  Solid = true
  Symmetric = false
FEATURE [Sketcher::SketchObject] Sketch024
  FullyConstrained = true
  sketch-geometry (7):
    g0: LineSegment StartX=0 StartY=0 StartZ=0 EndX=0 EndY=6 EndZ=0
    g1: Circle CenterX=0 CenterY=0 CenterZ=0 NormalX=0 NormalY=0 NormalZ=1 AngleXU=0 Radius=1
    g2: Circle CenterX=8 CenterY=6 CenterZ=0 NormalX=0 NormalY=0 NormalZ=1 AngleXU=0 Radius=1
    g3: BSplineCurve PolesCount=3 KnotsCount=2 Degree=2 IsPeriodic=0
    g4: GeomPoint X=0 Y=0 Z=0
    g5: GeomPoint X=8 Y=6 Z=0
    g6: LineSegment StartX=0 StartY=6 StartZ=0 EndX=8 EndY=6 EndZ=0
  constraints (14):
    c: Coincident(g0,g-1)
    c: Distance(g0) = 6
    c: Vertical(g0)
    c: Coincident(g3,g0)
    c: Weight(g1) = 1
    c: Equal(g1,g2)
    c: InternalAlignment(g1,g3)
    c: InternalAlignment(g2,g3)
    c: InternalAlignment(g4,g3)
    c: InternalAlignment(g5,g3)
    c: Block(g3)
    c: Coincident(g6,g0)
    c: Coincident(g6,g3)
    c: Horizontal(g6)
FEATURE [Part::Extrusion] Extrude018  label="caseScrewPillarBracket006"
  Base = -> Sketch024
  Dir = (0,0,1)
  DirMode = 2
  FaceMakerClass = Part::FaceMakerBullseye
  LengthFwd = 2.4
  LengthRev = 0
  Placement = pos=(103.7,29,6.77) rot=(0,-1,0;1.5708rad)
  Solid = true
  Symmetric = false
FEATURE [Sketcher::SketchObject] Sketch025
  FullyConstrained = true
  sketch-geometry (7):
    g0: LineSegment StartX=0 StartY=0 StartZ=0 EndX=0 EndY=6 EndZ=0
    g1: Circle CenterX=0 CenterY=0 CenterZ=0 NormalX=0 NormalY=0 NormalZ=1 AngleXU=0 Radius=1
    g2: Circle CenterX=8 CenterY=6 CenterZ=0 NormalX=0 NormalY=0 NormalZ=1 AngleXU=0 Radius=1
    g3: BSplineCurve PolesCount=3 KnotsCount=2 Degree=2 IsPeriodic=0
    g4: GeomPoint X=0 Y=0 Z=0
    g5: GeomPoint X=8 Y=6 Z=0
    g6: LineSegment StartX=0 StartY=6 StartZ=0 EndX=8 EndY=6 EndZ=0
  constraints (14):
    c: Coincident(g0,g-1)
    c: Distance(g0) = 6
    c: Vertical(g0)
    c: Coincident(g3,g0)
    c: Weight(g1) = 1
    c: Equal(g1,g2)
    c: InternalAlignment(g1,g3)
    c: InternalAlignment(g2,g3)
    c: InternalAlignment(g4,g3)
    c: InternalAlignment(g5,g3)
    c: Block(g3)
    c: Coincident(g6,g0)
    c: Coincident(g6,g3)
    c: Horizontal(g6)
FEATURE [Part::Extrusion] Extrude019  label="caseScrewPillarBracket007"
  Base = -> Sketch025
  Dir = (0,0,1)
  DirMode = 2
  FaceMakerClass = Part::FaceMakerBullseye
  LengthFwd = 2.4
  LengthRev = 0
  Placement = pos=(101.3,29,65.23) rot=(0,1,0;1.5708rad)
  Solid = true
  Symmetric = false
FEATURE [Part::Box] Box011  label="frontCaseScrewPillarBracket"
  AttacherType = Attacher::AttachEngine3D
  Height = 2.4
  Length = 16
  Placement = pos=(87,28,2.3) rot=(0,0,1;0rad)
  Width = 7
FEATURE [Part::Box] Box012  label="frontCaseScrewPillarBracket001"
  AttacherType = Attacher::AttachEngine3D
  Height = 2.4
  Length = 16
  Placement = pos=(87,28,67.3) rot=(0,0,1;0rad)
  Width = 7
FEATURE [Sketcher::SketchObject] Sketch026
  FullyConstrained = true
  sketch-geometry (17):
    g0: Circle CenterX=-3.5 CenterY=23.5 CenterZ=0 NormalX=0 NormalY=0 NormalZ=1 AngleXU=0 Radius=1
    g1: Circle CenterX=-1 CenterY=15.25 CenterZ=0 NormalX=0 NormalY=0 NormalZ=1 AngleXU=0 Radius=1
    g2: Circle CenterX=-3.5 CenterY=7 CenterZ=0 NormalX=0 NormalY=0 NormalZ=1 AngleXU=0 Radius=1
    g3: BSplineCurve PolesCount=3 KnotsCount=2 Degree=2 IsPeriodic=0
    g4: GeomPoint X=-3.5 Y=23.5 Z=0
    g5: GeomPoint X=-3.5 Y=7 Z=0
    g6: Circle CenterX=-4.8 CenterY=30.5 CenterZ=0 NormalX=0 NormalY=0 NormalZ=1 AngleXU=0 Radius=1
    g7: Circle CenterX=-3.5 CenterY=30.5 CenterZ=0 NormalX=0 NormalY=0 NormalZ=1 AngleXU=0 Radius=1
    g8: Circle CenterX=-3.5 CenterY=29.2 CenterZ=0 NormalX=0 NormalY=0 NormalZ=1 AngleXU=0 Radius=1
    g9: BSplineCurve PolesCount=3 KnotsCount=2 Degree=2 IsPeriodic=0
    g10: GeomPoint X=-4.8 Y=30.5 Z=0
    g11: GeomPoint X=-3.5 Y=29.2 Z=0
    g12: LineSegment StartX=-3.5 StartY=29.2 StartZ=0 EndX=-3.5 EndY=23.5 EndZ=0
    g13: LineSegment StartX=-4.8 StartY=30.5 StartZ=0 EndX=0 EndY=30.5 EndZ=0
    g14: LineSegment StartX=-3.5 StartY=5 StartZ=0 EndX=-3.5 EndY=7 EndZ=0
    g15: LineSegment StartX=0 StartY=5 StartZ=0 EndX=0 EndY=30.5 EndZ=0
    g16: LineSegment StartX=-3.5 StartY=5 StartZ=0 EndX=0 EndY=5 EndZ=0
  constraints (33):
    c: Weight(g0) = 1
    c: Equal(g0,g1)
    c: Equal(g0,g2)
    c: InternalAlignment(g0,g3)
    c: InternalAlignment(g1,g3)
    c: InternalAlignment(g2,g3)
    c: InternalAlignment(g4,g3)
    c: InternalAlignment(g5,g3)
    c: Block(g3)
    c: Weight(g6) = 1
    c: Equal(g6,g7)
    c: Equal(g6,g8)
    c: InternalAlignment(g6,g9)
    c: InternalAlignment(g7,g9)
    c: InternalAlignment(g8,g9)
    c: InternalAlignment(g10,g9)
    c: InternalAlignment(g11,g9)
    c: Block(g9)
    c: Coincident(g12,g9)
    c: Coincident(g12,g3)
    c: Vertical(g12)
    c: Coincident(g13,g9)
    c: Horizontal(g13)
    c: Distance(g13) = 4.8
    c: Coincident(g14,g3)
    c: Vertical(g14)
    c: Coincident(g15,g13)
    c: Vertical(g15)
    c: Tangent(g15,g1)
    c: Distance(g14) = 2
    c: Coincident(g16,g14)
    c: Horizontal(g16)
    c: Coincident(g15,g16)
FEATURE [Part::Feature] Face050
  shape: bbox 4.8 x 25.5 x 2e-07 mm, 1 faces, 0 solids (baked)
FEATURE [Part::Revolution] Revolve054  label="moreFrontCaseScrewPost001"
  Angle = 360
  Axis = (0,1,0)
  Base = (0,0,0)
  FaceMakerClass = Part::FaceMakerBullseye
  Placement = pos=(102.5,4.5,3.5) rot=(0,0,1;0rad)
  Solid = false
  Source = -> Face050
  Symmetric = false
FEATURE [Part::Feature] Face051
  shape: bbox 4.8 x 25.5 x 2e-07 mm, 1 faces, 0 solids (baked)
FEATURE [Part::Revolution] Revolve055  label="moreFrontCaseScrewPost002"
  Angle = 360
  Axis = (0,1,0)
  Base = (0,0,0)
  FaceMakerClass = Part::FaceMakerBullseye
  Placement = pos=(102.5,4.5,68.5) rot=(0,0,1;0rad)
  Solid = false
  Source = -> Face051
  Symmetric = false
FEATURE [Sketcher::SketchObject] Sketch027
  FullyConstrained = true
  sketch-geometry (10):
    g0: LineSegment StartX=-1.6 StartY=4.7 StartZ=0 EndX=-1.6 EndY=1.7 EndZ=0
    g1: LineSegment StartX=-3.5 StartY=4.7 StartZ=0 EndX=-1.6 EndY=4.7 EndZ=0
    g2: LineSegment StartX=-1.6 StartY=1.7 StartZ=0 EndX=-1.6 EndY=1.5 EndZ=0
    g3: LineSegment StartX=-1.6 StartY=1.5 StartZ=0 EndX=-5.2 EndY=1.5 EndZ=0
    g4: Circle CenterX=-3.5 CenterY=4.7 CenterZ=0 NormalX=0 NormalY=0 NormalZ=1 AngleXU=0 Radius=1
    g5: Circle CenterX=-3.59627 CenterY=2.99743 CenterZ=0 NormalX=0 NormalY=0 NormalZ=1 AngleXU=0 Radius=1
    g6: Circle CenterX=-5.2 CenterY=1.5 CenterZ=0 NormalX=0 NormalY=0 NormalZ=1 AngleXU=0 Radius=1
    g7: BSplineCurve PolesCount=3 KnotsCount=2 Degree=2 IsPeriodic=0
    g8: GeomPoint X=-3.5 Y=4.7 Z=0
    g9: GeomPoint X=-5.2 Y=1.5 Z=0
  constraints (23):
    c: Vertical(g0)
    c: Distance(g0) = 3
    c: Coincident(g1,g0)
    c: Horizontal(g1)
    c: Block(g0)
    c: Block(g1)
    c: Coincident(g2,g0)
    c: Vertical(g2)
    c: Distance(g2) = 0.2
    c: Coincident(g3,g2)
    c: Horizontal(g3)
    c: Block(g3)
    c: Coincident(g7,g1)
    c: Weight(g4) = 1
    c: Equal(g4,g5)
    c: Equal(g4,g6)
    c: Coincident(g7,g3)
    c: InternalAlignment(g4,g7)
    c: InternalAlignment(g5,g7)
    c: InternalAlignment(g6,g7)
    c: InternalAlignment(g8,g7)
    c: InternalAlignment(g9,g7)
    c: Block(g7)
FEATURE [Sketcher::SketchObject] Sketch028
  FullyConstrained = true
  sketch-geometry (18):
    g0: LineSegment StartX=0 StartY=3e-16 StartZ=0 EndX=0 EndY=1.7 EndZ=0
    g1: LineSegment StartX=-3.5 StartY=0 StartZ=0 EndX=-3.5 EndY=0.9 EndZ=0
    g2: Circle CenterX=-2.7 CenterY=1.7 CenterZ=0 NormalX=0 NormalY=0 NormalZ=1 AngleXU=0 Radius=1
    g3: Circle CenterX=-3.5 CenterY=1.7 CenterZ=0 NormalX=0 NormalY=0 NormalZ=1 AngleXU=0 Radius=1
    g4: Circle CenterX=-3.5 CenterY=0.9 CenterZ=0 NormalX=0 NormalY=0 NormalZ=1 AngleXU=0 Radius=1
    g5: BSplineCurve PolesCount=3 KnotsCount=2 Degree=2 IsPeriodic=0
    g6: GeomPoint X=-2.7 Y=1.7 Z=0
    g7: GeomPoint X=-3.5 Y=0.9 Z=0
    g8: LineSegment StartX=-3.5 StartY=0 StartZ=0 EndX=-3.5 EndY=-7 EndZ=0
    g9: LineSegment StartX=0 StartY=3e-16 StartZ=0 EndX=0 EndY=-7 EndZ=0
    g10: LineSegment StartX=-3.5 StartY=-7 StartZ=0 EndX=0 EndY=-7 EndZ=0
    g11: LineSegment StartX=-2.7 StartY=1.7 StartZ=0 EndX=-1.6 EndY=1.7 EndZ=0
    g12: LineSegment StartX=0 StartY=1.7 StartZ=0 EndX=0 EndY=4.5 EndZ=0
    g13: LineSegment StartX=0 StartY=4.5 StartZ=0 EndX=0 EndY=10.8 EndZ=0
    g14: LineSegment StartX=0 StartY=10.8 StartZ=0 EndX=-2 EndY=10.8 EndZ=0
    g15: LineSegment StartX=-1.6 StartY=4.7 StartZ=0 EndX=-1.6 EndY=1.7 EndZ=0
    g16: LineSegment StartX=-1.6 StartY=4.7 StartZ=0 EndX=-2 EndY=4.7 EndZ=0
    g17: LineSegment StartX=-2 StartY=4.7 StartZ=0 EndX=-2 EndY=10.8 EndZ=0
  constraints (44):
    c: Vertical(g0)
    c: Vertical(g1)
    c: Distance(g1) = 0.9
    c: Block(g0)
    c: Distance(g0) = 1.7
    c: Weight(g2) = 1
    c: Equal(g2,g3)
    c: Equal(g2,g4)
    c: Coincident(g5,g1)
    c: InternalAlignment(g2,g5)
    c: InternalAlignment(g3,g5)
    c: InternalAlignment(g4,g5)
    c: InternalAlignment(g6,g5)
    c: InternalAlignment(g7,g5)
    c: Block(g5)
    c: Coincident(g8,g1)
    c: Vertical(g8)
    c: Distance(g8) = 7
    c: Vertical(g9)
    c: Equal(g8,g9) = 7
    c: Coincident(g9,g0)
    c: Coincident(g10,g8)
    c: Coincident(g10,g9)
    c: Horizontal(g10)
    c: Coincident(g11,g5)
    c: Horizontal(g11)
    c: Coincident(g12,g0)
    c: Vertical(g12)
    c: Distance(g12) = 2.8
    c: Coincident(g13,g12)
    c: Vertical(g13)
    c: Distance(g13) = 6.3
    c: Coincident(g14,g13)
    c: Horizontal(g14)
    c: Distance(g14) = 2
    c: Vertical(g15)
    c: Distance(g15) = 3
    c: Block(g11)
    c: Coincident(g15,g11)
    c: Coincident(g16,g15)
    c: Horizontal(g16)
    c: Coincident(g17,g16)
    c: Coincident(g17,g14)
    c: Vertical(g17)
FEATURE [Part::Revolution] Revolve040  label="backCaseScrewRetainer001"
  Angle = 360
  Axis = (0,1,0)
  Base = (0,0,0)
  FaceMakerClass = Part::FaceMakerBullseye
  Placement = pos=(12.5,3,10) rot=(0,0,1;0rad)
  Solid = false
  Source = -> Face036
  Symmetric = false
FEATURE [Part::Feature] Face055
  shape: bbox 3.5 x 30.2 x 2e-07 mm, 1 faces, 0 solids (baked)
FEATURE [Part::Revolution] Revolve059  label="backCaseScrewPost"
  Angle = 360
  Axis = (0,1,0)
  Base = (0,0,0)
  FaceMakerClass = Part::FaceMakerBullseye
  Placement = pos=(12.5,4.5,10) rot=(0,0,1;0rad)
  Solid = false
  Source = -> Face055
  Symmetric = false
FEATURE [Part::Feature] Face056
  shape: bbox 3.5 x 30.2 x 2e-07 mm, 1 faces, 0 solids (baked)
FEATURE [Part::Revolution] Revolve060  label="backCaseScrewPost001"
  Angle = 360
  Axis = (0,1,0)
  Base = (0,0,0)
  FaceMakerClass = Part::FaceMakerBullseye
  Placement = pos=(12.5,4.5,62) rot=(0,0,1;0rad)
  Solid = false
  Source = -> Face056
  Symmetric = false
FEATURE [Part::Feature] Face057
  shape: bbox 3.5 x 17.8 x 2e-07 mm, 1 faces, 0 solids (baked)
FEATURE [Part::Revolution] Revolve061  label="removeToCreateScrewAndThreadedInsertHole"
  Angle = 360
  Axis = (0,1,0)
  Base = (0,0,0)
  FaceMakerClass = Part::FaceMakerBullseye
  Placement = pos=(12.5,0,10) rot=(0,0,1;0rad)
  Solid = false
  Source = -> Face057
  Symmetric = false
FEATURE [Part::Feature] Face058
  shape: bbox 3.5 x 17.8 x 2e-07 mm, 1 faces, 0 solids (baked)
FEATURE [Part::Revolution] Revolve062  label="removeToCreateScrewAndThreadedInsertHole001"
  Angle = 360
  Axis = (0,1,0)
  Base = (0,0,0)
  FaceMakerClass = Part::FaceMakerBullseye
  Placement = pos=(12.5,0,62) rot=(0,0,1;0rad)
  Solid = false
  Source = -> Face058
  Symmetric = false
FEATURE [Part::Feature] Face059
  shape: bbox 3.5 x 17.8 x 2e-07 mm, 1 faces, 0 solids (baked)
FEATURE [Part::Revolution] Revolve063  label="removeToCreateScrewAndThreadedInsertHole002"
  Angle = 360
  Axis = (0,1,0)
  Base = (0,0,0)
  FaceMakerClass = Part::FaceMakerBullseye
  Placement = pos=(89.5,0,68.5) rot=(0,0,1;0rad)
  Solid = false
  Source = -> Face059
  Symmetric = false
FEATURE [Part::Feature] Face060
  shape: bbox 3.5 x 17.8 x 2e-07 mm, 1 faces, 0 solids (baked)
FEATURE [Part::Revolution] Revolve064  label="removeToCreateScrewAndThreadedInsertHole003"
  Angle = 360
  Axis = (0,1,0)
  Base = (0,0,0)
  FaceMakerClass = Part::FaceMakerBullseye
  Placement = pos=(89.5,0,3.5) rot=(0,0,1;0rad)
  Solid = false
  Source = -> Face060
  Symmetric = false
FEATURE [Part::Feature] Face061
  shape: bbox 3.5 x 17.8 x 2e-07 mm, 1 faces, 0 solids (baked)
FEATURE [Part::Revolution] Revolve065  label="removeToCreateScrewAndThreadedInsertHole004"
  Angle = 360
  Axis = (0,1,0)
  Base = (0,0,0)
  FaceMakerClass = Part::FaceMakerBullseye
  Placement = pos=(102.5,4.7,3.5) rot=(0,0,1;0rad)
  Solid = false
  Source = -> Face061
  Symmetric = false
FEATURE [Part::Feature] Face062
  shape: bbox 3.5 x 17.8 x 2e-07 mm, 1 faces, 0 solids (baked)
FEATURE [Part::Revolution] Revolve066  label="removeToCreateScrewAndThreadedInsertHole005"
  Angle = 360
  Axis = (0,1,0)
  Base = (0,0,0)
  FaceMakerClass = Part::FaceMakerBullseye
  Placement = pos=(102.5,4.7,68.5) rot=(0,0,1;0rad)
  Solid = false
  Source = -> Face062
  Symmetric = false
FEATURE [Part::MultiFuse] Fusion047  label="makeHoles"
  Shapes = -> [Revolve066,Revolve065,Revolve064,Revolve063,Revolve062,Revolve061]
FEATURE [Part::Feature] Face063
  shape: bbox 3.6 x 3.2 x 2e-07 mm, 1 faces, 0 solids (baked)
FEATURE [Part::Revolution] Revolve067  label="moreFrontCaseScrewRetainer002"
  Angle = 360
  Axis = (0,1,0)
  Base = (0,0,0)
  FaceMakerClass = Part::FaceMakerBullseye
  Placement = pos=(102.5,4.5,68.5) rot=(0,0,1;0rad)
  Solid = false
  Source = -> Face063
  Symmetric = false
FEATURE [Part::Feature] Face064
  shape: bbox 3.6 x 3.2 x 2e-07 mm, 1 faces, 0 solids (baked)
FEATURE [Part::Revolution] Revolve068  label="moreFrontCaseScrewRetainer003"
  Angle = 360
  Axis = (0,1,0)
  Base = (0,0,0)
  FaceMakerClass = Part::FaceMakerBullseye
  Placement = pos=(102.5,4.5,3.5) rot=(0,0,1;0rad)
  Solid = false
  Source = -> Face064
  Symmetric = false
FEATURE [Part::Cut] Cut014  label="bottom003"
  Base = -> Cut007
  Tool = -> Fusion047
FEATURE [Part::Feature] Face065
  shape: bbox 3.5 x 17.8 x 2e-07 mm, 1 faces, 0 solids (baked)
FEATURE [Part::Revolution] Revolve069  label="removeToCreateScrewAndThreadedInsertHole006"
  Angle = 360
  Axis = (0,1,0)
  Base = (0,0,0)
  FaceMakerClass = Part::FaceMakerBullseye
  Placement = pos=(12.5,0,10) rot=(0,0,1;0rad)
  Solid = false
  Source = -> Face065
  Symmetric = false
FEATURE [Part::Feature] Face066
  shape: bbox 3.5 x 17.8 x 2e-07 mm, 1 faces, 0 solids (baked)
FEATURE [Part::Revolution] Revolve070  label="removeToCreateScrewAndThreadedInsertHole007"
  Angle = 360
  Axis = (0,1,0)
  Base = (0,0,0)
  FaceMakerClass = Part::FaceMakerBullseye
  Placement = pos=(12.5,0,62) rot=(0,0,1;0rad)
  Solid = false
  Source = -> Face066
  Symmetric = false
FEATURE [Part::Feature] Face067
  shape: bbox 3.5 x 17.8 x 2e-07 mm, 1 faces, 0 solids (baked)
FEATURE [Part::Revolution] Revolve071  label="removeToCreateScrewAndThreadedInsertHole008"
  Angle = 360
  Axis = (0,1,0)
  Base = (0,0,0)
  FaceMakerClass = Part::FaceMakerBullseye
  Placement = pos=(89.5,0,68.5) rot=(0,0,1;0rad)
  Solid = false
  Source = -> Face067
  Symmetric = false
FEATURE [Part::Feature] Face068
  shape: bbox 3.5 x 17.8 x 2e-07 mm, 1 faces, 0 solids (baked)
FEATURE [Part::Revolution] Revolve072  label="removeToCreateScrewAndThreadedInsertHole009"
  Angle = 360
  Axis = (0,1,0)
  Base = (0,0,0)
  FaceMakerClass = Part::FaceMakerBullseye
  Placement = pos=(89.5,0,3.5) rot=(0,0,1;0rad)
  Solid = false
  Source = -> Face068
  Symmetric = false
FEATURE [Part::Feature] Face069
  shape: bbox 3.5 x 17.8 x 2e-07 mm, 1 faces, 0 solids (baked)
FEATURE [Part::Feature] Face070
  shape: bbox 3.5 x 17.8 x 2e-07 mm, 1 faces, 0 solids (baked)
FEATURE [Part::Revolution] Revolve073  label="removeToCreateScrewAndThreadedInsertHole010"
  Angle = 360
  Axis = (0,1,0)
  Base = (0,0,0)
  FaceMakerClass = Part::FaceMakerBullseye
  Placement = pos=(102.5,4.7,3.5) rot=(0,0,1;0rad)
  Solid = false
  Source = -> Face069
  Symmetric = false
FEATURE [Part::Revolution] Revolve074  label="removeToCreateScrewAndThreadedInsertHole011"
  Angle = 360
  Axis = (0,1,0)
  Base = (0,0,0)
  FaceMakerClass = Part::FaceMakerBullseye
  Placement = pos=(102.5,4.7,68.5) rot=(0,0,1;0rad)
  Solid = false
  Source = -> Face070
  Symmetric = false
FEATURE [Part::MultiFuse] Fusion048  label="makeHoles001"
  Shapes = -> [Revolve074,Revolve073,Revolve072,Revolve071,Revolve070,Revolve069]
FEATURE [Part::MultiFuse] Fusion049  label="caseScrewRetainers"
  Shapes = -> [Revolve067,Revolve068,Revolve048,Revolve047,Revolve039,Revolve040]
FEATURE [Part::Cut] Cut015  label="caseScrewRetainers001"
  Base = -> Fusion049
  Tool = -> Fusion048
FEATURE [Part::MultiFuse] Fusion050  label="casePillars"
  Shapes = -> [Revolve055,Revolve054,Revolve043,Revolve046,Revolve059,Revolve060]
FEATURE [Part::Feature] Face071 .. Face076  x6 (patterned run collapsed; names and placements below)
  shape: bbox 3.5 x 17.8 x 2e-07 mm, 1 faces, 0 solids (baked)
FEATURE [Part::Revolution] Revolve075  label="removeToCreateScrewAndThreadedInsertHole012"
  Angle = 360
  Axis = (0,1,0)
  Base = (0,0,0)
  FaceMakerClass = Part::FaceMakerBullseye
  Placement = pos=(12.5,0,10) rot=(0,0,1;0rad)
  Solid = false
  Source = -> Face071
  Symmetric = false
FEATURE [Part::Revolution] Revolve076  label="removeToCreateScrewAndThreadedInsertHole013"
  Angle = 360
  Axis = (0,1,0)
  Base = (0,0,0)
  FaceMakerClass = Part::FaceMakerBullseye
  Placement = pos=(12.5,0,62) rot=(0,0,1;0rad)
  Solid = false
  Source = -> Face072
  Symmetric = false
FEATURE [Part::Revolution] Revolve077  label="removeToCreateScrewAndThreadedInsertHole014"
  Angle = 360
  Axis = (0,1,0)
  Base = (0,0,0)
  FaceMakerClass = Part::FaceMakerBullseye
  Placement = pos=(89.5,0,68.5) rot=(0,0,1;0rad)
  Solid = false
  Source = -> Face073
  Symmetric = false
FEATURE [Part::Revolution] Revolve078  label="removeToCreateScrewAndThreadedInsertHole015"
  Angle = 360
  Axis = (0,1,0)
  Base = (0,0,0)
  FaceMakerClass = Part::FaceMakerBullseye
  Placement = pos=(89.5,0,3.5) rot=(0,0,1;0rad)
  Solid = false
  Source = -> Face074
  Symmetric = false
FEATURE [Part::Revolution] Revolve079  label="removeToCreateScrewAndThreadedInsertHole016"
  Angle = 360
  Axis = (0,1,0)
  Base = (0,0,0)
  FaceMakerClass = Part::FaceMakerBullseye
  Placement = pos=(102.5,4.7,3.5) rot=(0,0,1;0rad)
  Solid = false
  Source = -> Face075
  Symmetric = false
FEATURE [Part::Revolution] Revolve080  label="removeToCreateScrewAndThreadedInsertHole017"
  Angle = 360
  Axis = (0,1,0)
  Base = (0,0,0)
  FaceMakerClass = Part::FaceMakerBullseye
  Placement = pos=(102.5,4.7,68.5) rot=(0,0,1;0rad)
  Solid = false
  Source = -> Face076
  Symmetric = false
FEATURE [Part::MultiFuse] Fusion051  label="makeHoles002"
  Shapes = -> [Revolve080,Revolve079,Revolve078,Revolve077,Revolve076,Revolve075]
FEATURE [Part::Cut] Cut016  label="caesPillars"
  Base = -> Fusion050
  Tool = -> Fusion051
FEATURE [Part::Revolution] Revolve009  label="plugHousing016"
  Angle = 360
  Axis = (0,1,0)
  Base = (0,0,0)
  FaceMakerClass = Part::FaceMakerBullseye
  Placement = pos=(0,0,36.15) rot=(0,0,1;0rad)
  Solid = false
  Source = -> Face012
  Symmetric = false
FEATURE [Part::MultiFuse] Fusion014  label="plugHousing023"
  Placement = pos=(0,0,0) rot=(0,0,1;1.5708rad)
  Shapes = -> [Revolve011,Revolve009]
FEATURE [Part::Revolution] Revolve010  label="plugHousing017"
  Angle = 360
  Axis = (0,1,0)
  Base = (0,0,0)
  FaceMakerClass = Part::FaceMakerBullseye
  Placement = pos=(0,0,36.15) rot=(0,0,1;0rad)
  Solid = false
  Source = -> Face014
  Symmetric = false
FEATURE [Part::MultiFuse] Fusion015  label="plugHousing024"
  Placement = pos=(0,0,0) rot=(0,0,1;1.5708rad)
  Shapes = -> [Revolve010,Revolve015]
FEATURE [Part::Revolution] Revolve014  label="plugHousing026"
  Angle = 360
  Axis = (0,1,0)
  Base = (0,0,0)
  FaceMakerClass = Part::FaceMakerBullseye
  Placement = pos=(0,0,36.15) rot=(0,0,1;0rad)
  Solid = false
  Source = -> Face011
  Symmetric = false
FEATURE [Part::Revolution] Revolve013  label="plugHousing025"
  Angle = 360
  Axis = (0,1,0)
  Base = (0,0,0)
  FaceMakerClass = Part::FaceMakerBullseye
  Placement = pos=(0,0,36.15) rot=(0,0,1;0rad)
  Solid = false
  Source = -> Face015
  Symmetric = false
FEATURE [Part::MultiFuse] Fusion016  label="plugHousing028"
  Placement = pos=(0,19,0) rot=(0,0,1;3.14159rad)
  Shapes = -> [Fusion014,Fusion013]
FEATURE [Part::MultiFuse] Fusion011  label="plugHousing018"
  Placement = pos=(0,0,0) rot=(0,0,1;1.5708rad)
  Shapes = -> [Revolve014,Revolve013]
FEATURE [Part::MultiFuse] Fusion012  label="plugHousing019"
  Placement = pos=(0,19,0) rot=(0,0,1;3.14159rad)
  Shapes = -> [Fusion011,Fusion015]
FEATURE [Part::MultiFuse] Fusion017  label="plugHousing029"
  Placement = pos=(122.621,0,-0.15) rot=(0,0,1;0rad)
  Shapes = -> [Fusion016,Fusion012]
FEATURE [Part::MultiFuse] Fusion052  label="casePillarRetainers"
  Shapes = -> [Extrude012,Extrude013,Extrude014,Extrude015,Extrude016,Extrude017,Extrude018,Extrude019,Box011,Box012]
FEATURE [Part::Feature] Face077
  shape: bbox 3.5 x 17.8 x 2e-07 mm, 1 faces, 0 solids (baked)
FEATURE [Part::Revolution] Revolve081  label="removeToCreateScrewAndThreadedInsertHole018"
  Angle = 360
  Axis = (0,1,0)
  Base = (0,0,0)
  FaceMakerClass = Part::FaceMakerBullseye
  Placement = pos=(62.3,30.3,19.7) rot=(0,0,1;0rad)
  Solid = false
  Source = -> Face077
  Symmetric = false
FEATURE [Part::Feature] Face078
  shape: bbox 3.5 x 17.8 x 2e-07 mm, 1 faces, 0 solids (baked)
FEATURE [Part::Revolution] Revolve082  label="removeToCreateScrewAndThreadedInsertHole019"
  Angle = 360
  Axis = (0,1,0)
  Base = (0,0,0)
  FaceMakerClass = Part::FaceMakerBullseye
  Placement = pos=(62.3,30.3,51.7) rot=(0,0,1;0rad)
  Solid = false
  Source = -> Face078
  Symmetric = false
FEATURE [Part::Feature] Face079
  shape: bbox 3.5 x 17.8 x 2e-07 mm, 1 faces, 0 solids (baked)
FEATURE [Part::Revolution] Revolve083  label="removeToCreateScrewAndThreadedInsertHole020"
  Angle = 360
  Axis = (0,1,0)
  Base = (0,0,0)
  FaceMakerClass = Part::FaceMakerBullseye
  Placement = pos=(30.3,30.3,19.7) rot=(0,0,1;0rad)
  Solid = false
  Source = -> Face079
  Symmetric = false
FEATURE [Part::Feature] Face080
  shape: bbox 3.5 x 17.8 x 2e-07 mm, 1 faces, 0 solids (baked)
FEATURE [Part::Revolution] Revolve084  label="removeToCreateScrewAndThreadedInsertHole021"
  Angle = 360
  Axis = (0,1,0)
  Base = (0,0,0)
  FaceMakerClass = Part::FaceMakerBullseye
  Placement = pos=(30.3,30.3,51.7) rot=(0,0,1;0rad)
  Solid = false
  Source = -> Face080
  Symmetric = false
FEATURE [Part::MultiFuse] Fusion053  label="createThreadedInsertHolesForFan"
  Shapes = -> [Revolve081,Revolve082,Revolve083,Revolve084]
FEATURE [Part::Cut] Cut017  label="fanScrewHousing001"
  Base = -> Fusion046
  Tool = -> Fusion053
FEATURE [Part::Feature] Face081
  shape: bbox 3.5 x 17.8 x 2e-07 mm, 1 faces, 0 solids (baked)
FEATURE [Part::Revolution] Revolve085  label="removeToCreateScrewAndThreadedInsertHole022"
  Angle = 360
  Axis = (0,1,0)
  Base = (0,0,0)
  FaceMakerClass = Part::FaceMakerBullseye
  Placement = pos=(62.3,30.3,19.7) rot=(0,0,1;0rad)
  Solid = false
  Source = -> Face081
  Symmetric = false
FEATURE [Part::Feature] Face082
  shape: bbox 3.5 x 17.8 x 2e-07 mm, 1 faces, 0 solids (baked)
FEATURE [Part::Revolution] Revolve086  label="removeToCreateScrewAndThreadedInsertHole023"
  Angle = 360
  Axis = (0,1,0)
  Base = (0,0,0)
  FaceMakerClass = Part::FaceMakerBullseye
  Placement = pos=(62.3,30.3,51.7) rot=(0,0,1;0rad)
  Solid = false
  Source = -> Face082
  Symmetric = false
FEATURE [Part::Feature] Face083
  shape: bbox 3.5 x 17.8 x 2e-07 mm, 1 faces, 0 solids (baked)
FEATURE [Part::Revolution] Revolve087  label="removeToCreateScrewAndThreadedInsertHole024"
  Angle = 360
  Axis = (0,1,0)
  Base = (0,0,0)
  FaceMakerClass = Part::FaceMakerBullseye
  Placement = pos=(30.3,30.3,19.7) rot=(0,0,1;0rad)
  Solid = false
  Source = -> Face083
  Symmetric = false
FEATURE [Part::Feature] Face084
  shape: bbox 3.5 x 17.8 x 2e-07 mm, 1 faces, 0 solids (baked)
FEATURE [Part::Revolution] Revolve088  label="removeToCreateScrewAndThreadedInsertHole025"
  Angle = 360
  Axis = (0,1,0)
  Base = (0,0,0)
  FaceMakerClass = Part::FaceMakerBullseye
  Placement = pos=(30.3,30.3,51.7) rot=(0,0,1;0rad)
  Solid = false
  Source = -> Face084
  Symmetric = false
FEATURE [Part::MultiFuse] Fusion054  label="createThreadedInsertHolesForFan001"
  Shapes = -> [Revolve085,Revolve086,Revolve087,Revolve088]
FEATURE [Part::Cut] Cut018  label="top007"
  Base = -> Fusion040
  Tool = -> Fusion054
FEATURE [Sketcher::SketchObject] Sketch029
  FullyConstrained = false
  Placement = pos=(0,0,0) rot=(1,0,0;1.5708rad)
  sketch-geometry (24):
    g0: ArcOfCircle CenterX=-4 CenterY=-10.5 CenterZ=0 NormalX=0 NormalY=0 NormalZ=1 AngleXU=0 Radius=1.5 StartAngle=6e-16 EndAngle=3.14159
    g1: ArcOfCircle CenterX=-34.2 CenterY=-10.5 CenterZ=0 NormalX=0 NormalY=0 NormalZ=1 AngleXU=0 Radius=1.5 StartAngle=0 EndAngle=3.14159
    g2: ArcOfCircle CenterX=-34.2 CenterY=-27.7 CenterZ=0 NormalX=0 NormalY=0 NormalZ=1 AngleXU=0 Radius=1.5 StartAngle=3.14159 EndAngle=6.28319
    g3: ArcOfCircle CenterX=-4 CenterY=-27.7 CenterZ=0 NormalX=0 NormalY=0 NormalZ=1 AngleXU=0 Radius=1.5 StartAngle=3.1416 EndAngle=6.28319
    g4: ArcOfCircle CenterX=-10 CenterY=-4.3 CenterZ=0 NormalX=0 NormalY=0 NormalZ=1 AngleXU=0 Radius=1.5 StartAngle=2e-16 EndAngle=3.14159
    g5: ArcOfCircle CenterX=-16.1 CenterY=-1.8 CenterZ=0 NormalX=0 NormalY=0 NormalZ=1 AngleXU=0 Radius=1.5 StartAngle=5e-16 EndAngle=3.14159
    g6: ArcOfCircle CenterX=-22.1 CenterY=-1.8 CenterZ=0 NormalX=0 NormalY=0 NormalZ=1 AngleXU=0 Radius=1.5 StartAngle=5e-16 EndAngle=3.14159
    g7: ArcOfCircle CenterX=-28.2 CenterY=-4.3 CenterZ=0 NormalX=0 NormalY=0 NormalZ=1 AngleXU=0 Radius=1.5 StartAngle=2e-16 EndAngle=3.14159
    g8: ArcOfCircle CenterX=-10 CenterY=-33.9 CenterZ=0 NormalX=0 NormalY=0 NormalZ=1 AngleXU=0 Radius=1.5 StartAngle=3.14159 EndAngle=6.28319
    g9: ArcOfCircle CenterX=-16.1 CenterY=-36.4 CenterZ=0 NormalX=0 NormalY=0 NormalZ=1 AngleXU=0 Radius=1.5 StartAngle=3.14159 EndAngle=6.28319
    g10: ArcOfCircle CenterX=-22.1 CenterY=-36.4 CenterZ=0 NormalX=0 NormalY=0 NormalZ=1 AngleXU=0 Radius=1.5 StartAngle=3.14159 EndAngle=6.28319
    g11: ArcOfCircle CenterX=-28.2 CenterY=-33.9 CenterZ=0 NormalX=0 NormalY=0 NormalZ=1 AngleXU=0 Radius=1.5 StartAngle=3.14159 EndAngle=6.28319
    g12: LineSegment StartX=-35.7 StartY=-10.5 StartZ=0 EndX=-35.7 EndY=-27.7 EndZ=0
    g13: LineSegment StartX=-32.7 StartY=-10.5 StartZ=0 EndX=-32.7 EndY=-27.7 EndZ=0
    g14: LineSegment StartX=-29.7 StartY=-33.9 StartZ=0 EndX=-29.7 EndY=-4.3 EndZ=0
    g15: LineSegment StartX=-26.7 StartY=-33.9 StartZ=0 EndX=-26.7 EndY=-4.3 EndZ=0
    g16: LineSegment StartX=-2.5 StartY=-10.5 StartZ=0 EndX=-2.5 EndY=-27.7 EndZ=0
    g17: LineSegment StartX=-8.5 StartY=-4.3 StartZ=0 EndX=-8.5 EndY=-33.9 EndZ=0
    g18: LineSegment StartX=-5.5 StartY=-10.5 StartZ=0 EndX=-5.5 EndY=-27.7 EndZ=0
    g19: LineSegment StartX=-11.5 StartY=-4.3 StartZ=0 EndX=-11.5 EndY=-33.9 EndZ=0
    g20: LineSegment StartX=-14.6 StartY=-1.8 StartZ=0 EndX=-14.6 EndY=-36.4 EndZ=0
    g21: LineSegment StartX=-17.6 StartY=-1.8 StartZ=0 EndX=-17.6 EndY=-36.4 EndZ=0
    g22: LineSegment StartX=-20.6 StartY=-36.4 StartZ=0 EndX=-20.6 EndY=-1.8 EndZ=0
    g23: LineSegment StartX=-23.6 StartY=-1.8 StartZ=0 EndX=-23.6 EndY=-36.4 EndZ=0
  constraints (48):
    c: Block(g0)
    c: Block(g1)
    c: Block(g2)
    c: Block(g3)
    c: Block(g4)
    c: Block(g5)
    c: Block(g6)
    c: Block(g7)
    c: Block(g8)
    c: Block(g9)
    c: Block(g10)
    c: Block(g11)
    c: Coincident(g12,g1)
    c: Coincident(g12,g2)
    c: Vertical(g12)
    c: Coincident(g13,g1)
    c: Coincident(g13,g2)
    c: Vertical(g13)
    c: Coincident(g14,g11)
    c: Coincident(g14,g7)
    c: Vertical(g14)
    c: Coincident(g15,g11)
    c: Coincident(g15,g7)
    c: Vertical(g15)
    c: Coincident(g16,g0)
    c: Coincident(g16,g3)
    c: Vertical(g16)
    c: Coincident(g17,g4)
    c: Coincident(g17,g8)
    c: Vertical(g17)
    c: Coincident(g18,g0)
    c: Coincident(g18,g3)
    c: Vertical(g18)
    c: Coincident(g19,g4)
    c: Coincident(g19,g8)
    c: Vertical(g19)
    c: Coincident(g20,g5)
    c: Coincident(g20,g9)
    c: Vertical(g20)
    c: Coincident(g21,g5)
    c: Coincident(g21,g9)
    c: Vertical(g21)
    c: Coincident(g22,g10)
    c: Coincident(g22,g6)
    c: Vertical(g22)
    c: Coincident(g23,g6)
    c: Coincident(g23,g10)
    c: Vertical(g23)
FEATURE [Part::Extrusion] Extrude020  label="removeToCreateFanGrillHoles"
  Base = -> Sketch029
  Dir = (0,-1,6e-16)
  DirMode = 2
  FaceMakerClass = Part::FaceMakerBullseye
  LengthFwd = 10
  LengthRev = 0
  Placement = pos=(65.4,44,54.82) rot=(0,0,1;0rad)
  Solid = true
  Symmetric = false
FEATURE [Part::MultiFuse] Fusion055  label="top008"
  Shapes = -> [Cut017,Cut018]
FEATURE [Part::Cut] Cut019  label="top009"
  Base = -> Fusion055
  Tool = -> Extrude020
FEATURE [App::MeasureDistance] Distance003  label="Distance: 71.95 mm"
  Distance = 71.9513
  P1 = (117,38,72)
  P2 = (117,38,0.0487319)
FEATURE [Sketcher::SketchObject] Sketch030
  FullyConstrained = true
  Placement = pos=(0,0,0) rot=(0.57735,0.57735,0.57735;2.0944rad)
  sketch-geometry (30):
    g0: LineSegment StartX=-3.1e-15 StartY=0 StartZ=0 EndX=-3.1e-15 EndY=19 EndZ=0
    g1: LineSegment StartX=0 StartY=53 StartZ=0 EndX=0 EndY=72 EndZ=0
    g2: ArcOfCircle CenterX=0 CenterY=36 CenterZ=0 NormalX=0 NormalY=0 NormalZ=1 AngleXU=0 Radius=17 StartAngle=1.5708 EndAngle=4.71239
    g3: LineSegment StartX=0 StartY=72 StartZ=0 EndX=-49.19 EndY=72 EndZ=0
    g4: LineSegment StartX=-3.1e-15 StartY=0 StartZ=0 EndX=-49.19 EndY=0 EndZ=0
    g5: LineSegment StartX=-49.19 StartY=69.25 StartZ=0 EndX=-49.19 EndY=66.25 EndZ=0
    g6: LineSegment StartX=-49.19 StartY=66.25 StartZ=0 EndX=-49.19 EndY=63.5 EndZ=0
    g7: LineSegment StartX=-49.19 StartY=63.5 StartZ=0 EndX=-49.19 EndY=60.5 EndZ=0
    g8: LineSegment StartX=-49.19 StartY=72 StartZ=0 EndX=-49.19 EndY=69.25 EndZ=0
    g9: LineSegment StartX=-49.19 StartY=57.75 StartZ=0 EndX=-49.19 EndY=54.75 EndZ=0
    g10: LineSegment StartX=-49.19 StartY=54.75 StartZ=0 EndX=-49.19 EndY=52 EndZ=0
    g11: LineSegment StartX=-49.19 StartY=52 StartZ=0 EndX=-49.19 EndY=49 EndZ=0
    g12: LineSegment StartX=-49.19 StartY=60.5 StartZ=0 EndX=-49.19 EndY=57.75 EndZ=0
    g13: LineSegment StartX=-49.19 StartY=46.25 StartZ=0 EndX=-49.19 EndY=43.25 EndZ=0
    g14: LineSegment StartX=-49.19 StartY=43.25 StartZ=0 EndX=-49.19 EndY=40.5 EndZ=0
    g15: LineSegment StartX=-49.19 StartY=40.5 StartZ=0 EndX=-49.19 EndY=37.5 EndZ=0
    g16: LineSegment StartX=-49.19 StartY=49 StartZ=0 EndX=-49.19 EndY=46.25 EndZ=0
    g17: LineSegment StartX=-49.19 StartY=34.5 StartZ=0 EndX=-49.19 EndY=31.5 EndZ=0
    g18: LineSegment StartX=-49.19 StartY=31.5 StartZ=0 EndX=-49.19 EndY=28.75 EndZ=0
    g19: LineSegment StartX=-49.19 StartY=28.75 StartZ=0 EndX=-49.19 EndY=25.75 EndZ=0
    g20: LineSegment StartX=-49.19 StartY=23 StartZ=0 EndX=-49.19 EndY=20 EndZ=0
    g21: LineSegment StartX=-49.19 StartY=20 StartZ=0 EndX=-49.19 EndY=17.25 EndZ=0
    g22: LineSegment StartX=-49.19 StartY=17.25 StartZ=0 EndX=-49.19 EndY=14.25 EndZ=0
    g23: LineSegment StartX=-49.19 StartY=25.75 StartZ=0 EndX=-49.19 EndY=23 EndZ=0
    g24: LineSegment StartX=-49.19 StartY=11.5 StartZ=0 EndX=-49.19 EndY=8.5 EndZ=0
    g25: LineSegment StartX=-49.19 StartY=8.5 StartZ=0 EndX=-49.19 EndY=5.75 EndZ=0
    g26: LineSegment StartX=-49.19 StartY=5.75 StartZ=0 EndX=-49.19 EndY=2.75 EndZ=0
    g27: LineSegment StartX=-49.19 StartY=14.25 StartZ=0 EndX=-49.19 EndY=11.5 EndZ=0
    g28: LineSegment StartX=-49.19 StartY=37.5 StartZ=0 EndX=-49.19 EndY=34.5 EndZ=0
    g29: LineSegment StartX=-49.19 StartY=2.75 StartZ=0 EndX=-49.19 EndY=0 EndZ=0
  constraints (94):
    c: Coincident(g0,g-1)
    c: Distance(g0) = 19
    c: Vertical(g0)
    c: Equal(g0,g1) = 22
    c: Vertical(g1)
    c: Coincident(g2,g0)
    c: Block(g1)
    c: Block(g2)
    c: Coincident(g3,g1)
    c: Horizontal(g3)
    c: Distance(g3) = 49.19
    c: Coincident(g4,g0)
    c: Horizontal(g4)
    c: Block(g4)
    c: Vertical(g5)
    c: Distance(g5) = 3
    c: Block(g5)
    c: Coincident(g6,g5)
    c: Vertical(g6)
    c: Distance(g6) = 2.75
    c: Coincident(g7,g6)
    c: Vertical(g7)
    c: Distance(g7) = 3
    c: Coincident(g8,g3)
    c: Coincident(g8,g5)
    c: Vertical(g8)
    c: Distance(g8) = 2.75
    c: Vertical(g9)
    c: Equal(g5,g9) = 3
    c: Block(g9)
    c: Coincident(g10,g9)
    c: Vertical(g10)
    c: Equal(g6,g10) = 2.75
    c: Coincident(g11,g10)
    c: Vertical(g11)
    c: Equal(g7,g11) = 3
    c: Coincident(g12,g9)
    c: Vertical(g12)
    c: Equal(g8,g12) = 2.75
    c: Coincident(g12,g7)
    c: Vertical(g13)
    c: Equal(g5,g13) = 3
    c: Block(g13)
    c: Coincident(g14,g13)
    c: Vertical(g14)
    c: Equal(g6,g14) = 2.75
    c: Coincident(g15,g14)
    c: Vertical(g15)
    c: Equal(g7,g15) = 3
    c: Coincident(g16,g13)
    c: Vertical(g16)
    c: Equal(g8,g16) = 2.75
    c: Coincident(g16,g11)
    c: Vertical(g17)
    c: Equal(g5,g17) = 3
    c: Block(g17)
    c: Coincident(g18,g17)
    c: Vertical(g18)
    c: Equal(g6,g18) = 2.75
    c: Coincident(g19,g18)
    c: Vertical(g19)
    c: Equal(g7,g19) = 3
    c: Vertical(g20)
    c: Equal(g5,g20) = 3
    c: Block(g20)
    c: Coincident(g21,g20)
    c: Vertical(g21)
    c: Equal(g6,g21) = 2.75
    c: Coincident(g22,g21)
    c: Vertical(g22)
    c: Equal(g7,g22) = 3
    c: Coincident(g23,g20)
    c: Vertical(g23)
    c: Equal(g8,g23) = 2.75
    c: Coincident(g23,g19)
    c: Vertical(g24)
    c: Equal(g5,g24) = 3
    c: Block(g24)
    c: Coincident(g25,g24)
    c: Vertical(g25)
    c: Equal(g6,g25) = 2.75
    c: Coincident(g26,g25)
    c: Vertical(g26)
    c: Equal(g7,g26) = 3
    c: Coincident(g27,g24)
    c: Vertical(g27)
    c: Equal(g8,g27) = 2.75
    c: Coincident(g27,g22)
    c: Coincident(g28,g15)
    c: Coincident(g28,g17)
    c: Distance(g28) = 3
    c: Coincident(g29,g26)
    c: Coincident(g29,g4)
    c: Vertical(g29)
